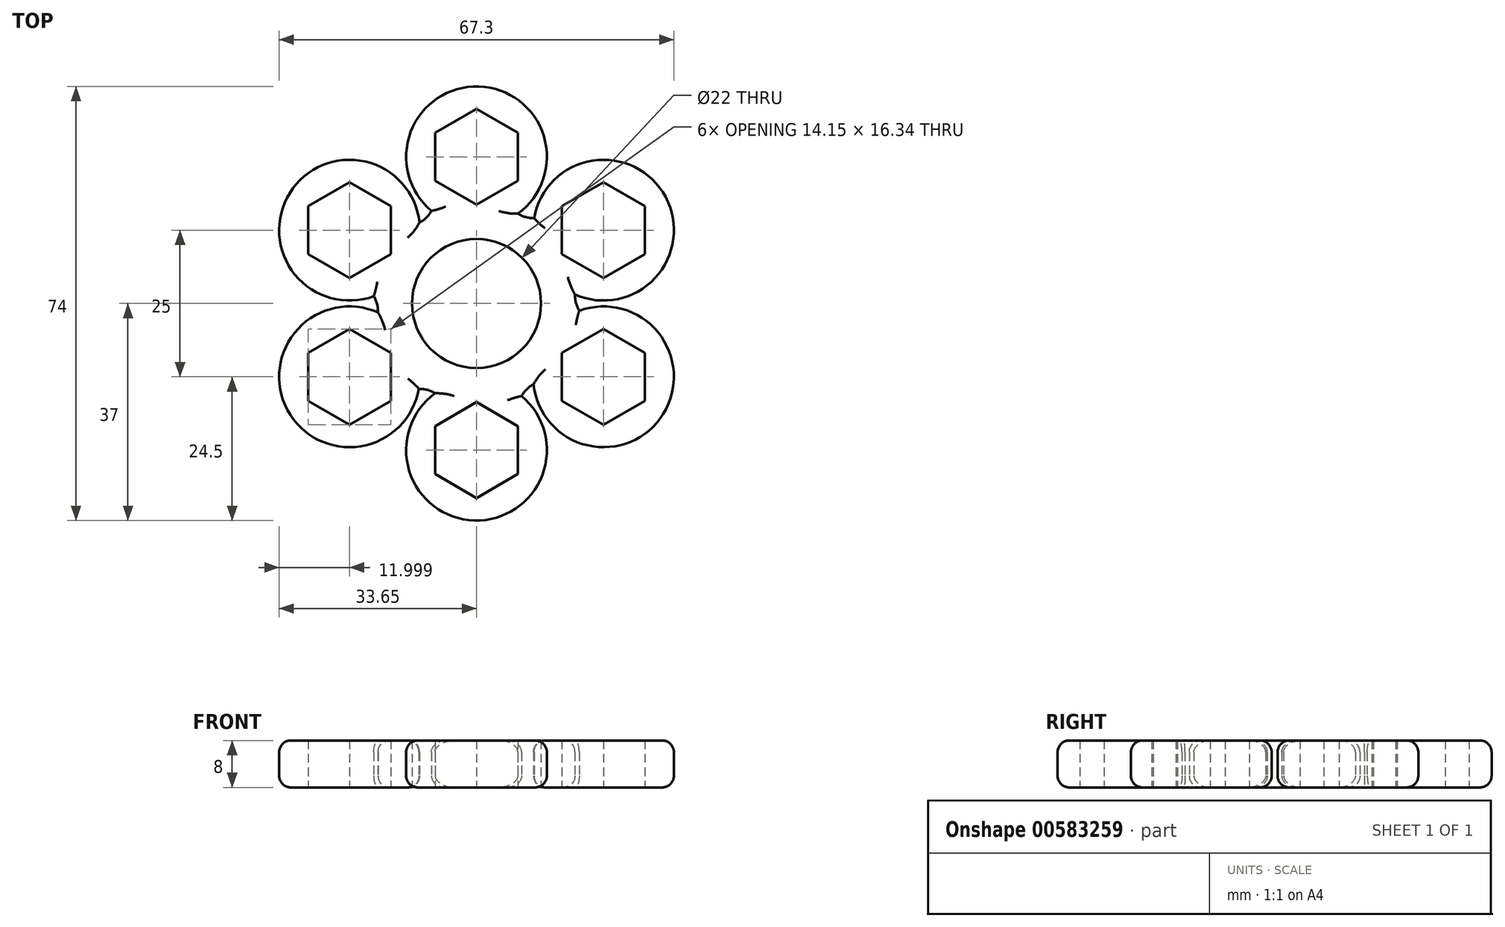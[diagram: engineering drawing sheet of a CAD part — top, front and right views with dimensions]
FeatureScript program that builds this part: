
annotation { "Feature Type Name" : "Feature", "Feature Type Description" : "" }
export const myFeature = defineFeature(function(context is Context, id is Id, definition is map)
    precondition{}
    {
        {
            var Q0;
            Q0=qCreatedBy(makeId("Top.planeOp"),FACE);
            var sketch = newSketch(context, id + "F0", { "sketchPlane" : qUnion([Q0])});
            skCircle(sketch, "E0", {"center": v(0, 0) * mm, "radius": 11 * mm});
            skCircle(sketch, "E1.cCircle", {"center": v(0, 25) * mm, "radius": 7.07 * mm, "construction": true});
            skLineSegment(sketch, "E1.0", {"start": v(7.07, 20.92) * mm, "end": v(0, 16.83) * mm});
            skLineSegment(sketch, "E1.1", {"start": v(0, 16.83) * mm, "end": v(-7.08, 20.92) * mm});
            skLineSegment(sketch, "E1.2", {"start": v(-7.08, 20.92) * mm, "end": v(-7.08, 29.08) * mm});
            skLineSegment(sketch, "E1.3", {"start": v(-7.08, 29.08) * mm, "end": v(0, 33.17) * mm});
            skLineSegment(sketch, "E1.4", {"start": v(0, 33.17) * mm, "end": v(7.08, 29.08) * mm});
            skLineSegment(sketch, "E1.5", {"start": v(7.07, 29.08) * mm, "end": v(7.07, 20.92) * mm});
            skPoint(sketch, "E1.0.midPoint", {"position": v(3.54, 18.87) * mm});
            skArc(sketch, "E2", {"start": v(7.08, 15.3) * mm, "mid": v(0, 37) * mm, "end": v(-7.08, 15.3) * mm});
            skLineSegment(sketch, "E3", {"start": v(-7.08, 15.3) * mm, "end": v(-7.08, 12.25) * mm});
            skLineSegment(sketch, "E4", {"start": v(7.08, 12.25) * mm, "end": v(7.08, 15.3) * mm});
            skPoint(sketch, "E5.orphan", {"position": v(7.07, 8.42) * mm});
            skLineSegment(sketch, "E6.1.0", {"start": v(-16.8, 1.53) * mm, "end": v(-14.15, 0) * mm});
            skArc(sketch, "E6.1.1", {"start": v(-9.72, 13.78) * mm, "mid": v(-32.04, 18.5) * mm, "end": v(-16.8, 1.53) * mm});
            skLineSegment(sketch, "E6.1.2", {"start": v(-7.08, 12.25) * mm, "end": v(-9.72, 13.78) * mm});
            skLineSegment(sketch, "E6.1.3", {"start": v(-14.58, 16.58) * mm, "end": v(-14.58, 8.42) * mm});
            skLineSegment(sketch, "E6.1.4", {"start": v(-14.58, 8.42) * mm, "end": v(-21.65, 4.33) * mm});
            skLineSegment(sketch, "E6.1.5", {"start": v(-21.65, 4.33) * mm, "end": v(-28.73, 8.42) * mm});
            skLineSegment(sketch, "E6.1.6", {"start": v(-28.73, 8.42) * mm, "end": v(-28.73, 16.58) * mm});
            skLineSegment(sketch, "E6.1.7", {"start": v(-28.73, 16.58) * mm, "end": v(-21.65, 20.67) * mm});
            skLineSegment(sketch, "E6.1.8", {"start": v(-21.65, 20.67) * mm, "end": v(-14.58, 16.58) * mm});
            skLineSegment(sketch, "E6.2.0", {"start": v(-9.72, -13.78) * mm, "end": v(-7.08, -12.25) * mm});
            skArc(sketch, "E6.2.1", {"start": v(-16.8, -1.53) * mm, "mid": v(-32.04, -18.5) * mm, "end": v(-9.72, -13.78) * mm});
            skLineSegment(sketch, "E6.2.2", {"start": v(-14.15, 0) * mm, "end": v(-16.8, -1.53) * mm});
            skLineSegment(sketch, "E6.2.3", {"start": v(-21.65, -4.33) * mm, "end": v(-14.58, -8.42) * mm});
            skLineSegment(sketch, "E6.2.4", {"start": v(-14.58, -8.42) * mm, "end": v(-14.58, -16.58) * mm});
            skLineSegment(sketch, "E6.2.5", {"start": v(-14.58, -16.58) * mm, "end": v(-21.65, -20.67) * mm});
            skLineSegment(sketch, "E6.2.6", {"start": v(-21.65, -20.67) * mm, "end": v(-28.73, -16.58) * mm});
            skLineSegment(sketch, "E6.2.7", {"start": v(-28.73, -16.58) * mm, "end": v(-28.73, -8.42) * mm});
            skLineSegment(sketch, "E6.2.8", {"start": v(-28.73, -8.42) * mm, "end": v(-21.65, -4.33) * mm});
            skLineSegment(sketch, "E6.3.0", {"start": v(7.08, -15.3) * mm, "end": v(7.08, -12.25) * mm});
            skArc(sketch, "E6.3.1", {"start": v(-7.08, -15.3) * mm, "mid": v(0, -37) * mm, "end": v(7.07, -15.3) * mm});
            skLineSegment(sketch, "E6.3.2", {"start": v(-7.08, -12.25) * mm, "end": v(-7.08, -15.3) * mm});
            skLineSegment(sketch, "E6.3.3", {"start": v(-7.08, -20.92) * mm, "end": v(0, -16.83) * mm});
            skLineSegment(sketch, "E6.3.4", {"start": v(0, -16.83) * mm, "end": v(7.07, -20.92) * mm});
            skLineSegment(sketch, "E6.3.5", {"start": v(7.08, -20.92) * mm, "end": v(7.08, -29.08) * mm});
            skLineSegment(sketch, "E6.3.6", {"start": v(7.07, -29.08) * mm, "end": v(0, -33.17) * mm});
            skLineSegment(sketch, "E6.3.7", {"start": v(0, -33.17) * mm, "end": v(-7.08, -29.08) * mm});
            skLineSegment(sketch, "E6.3.8", {"start": v(-7.08, -29.08) * mm, "end": v(-7.08, -20.92) * mm});
            skLineSegment(sketch, "E6.4.0", {"start": v(16.8, -1.53) * mm, "end": v(14.15, 0) * mm});
            skArc(sketch, "E6.4.1", {"start": v(9.72, -13.78) * mm, "mid": v(32.04, -18.5) * mm, "end": v(16.8, -1.53) * mm});
            skLineSegment(sketch, "E6.4.2", {"start": v(7.08, -12.25) * mm, "end": v(9.72, -13.78) * mm});
            skLineSegment(sketch, "E6.4.3", {"start": v(14.58, -16.58) * mm, "end": v(14.58, -8.42) * mm});
            skLineSegment(sketch, "E6.4.4", {"start": v(14.58, -8.42) * mm, "end": v(21.65, -4.33) * mm});
            skLineSegment(sketch, "E6.4.5", {"start": v(21.65, -4.33) * mm, "end": v(28.73, -8.42) * mm});
            skLineSegment(sketch, "E6.4.6", {"start": v(28.73, -8.42) * mm, "end": v(28.73, -16.58) * mm});
            skLineSegment(sketch, "E6.4.7", {"start": v(28.73, -16.58) * mm, "end": v(21.65, -20.67) * mm});
            skLineSegment(sketch, "E6.4.8", {"start": v(21.65, -20.67) * mm, "end": v(14.58, -16.58) * mm});
            skLineSegment(sketch, "E6.5.0", {"start": v(9.72, 13.78) * mm, "end": v(7.08, 12.25) * mm});
            skArc(sketch, "E6.5.1", {"start": v(16.8, 1.53) * mm, "mid": v(32.04, 18.5) * mm, "end": v(9.72, 13.78) * mm});
            skLineSegment(sketch, "E6.5.2", {"start": v(14.15, 0) * mm, "end": v(16.8, 1.53) * mm});
            skLineSegment(sketch, "E6.5.3", {"start": v(21.65, 4.33) * mm, "end": v(14.58, 8.42) * mm});
            skLineSegment(sketch, "E6.5.4", {"start": v(14.58, 8.42) * mm, "end": v(14.58, 16.58) * mm});
            skLineSegment(sketch, "E6.5.5", {"start": v(14.58, 16.58) * mm, "end": v(21.65, 20.67) * mm});
            skLineSegment(sketch, "E6.5.6", {"start": v(21.65, 20.67) * mm, "end": v(28.73, 16.58) * mm});
            skLineSegment(sketch, "E6.5.7", {"start": v(28.73, 16.58) * mm, "end": v(28.73, 8.42) * mm});
            skLineSegment(sketch, "E6.5.8", {"start": v(28.73, 8.42) * mm, "end": v(21.65, 4.33) * mm});
            skPoint(sketch, "E7.orphan", {"position": v(6.92, 12.17) * mm});
            skPoint(sketch, "E8.orphan", {"position": v(7.08, 12.08) * mm});
            skPoint(sketch, "E9.orphan", {"position": v(14, -0.09) * mm});
            skPoint(sketch, "E10.orphan", {"position": v(7.08, -12.08) * mm});
            skPoint(sketch, "E11.orphan", {"position": v(-14, 0.09) * mm});
            skSolve(sketch);
        }
        {
            var Q0;
            Q0=makeQuery(id+"F0.imprint","IMPRINT",FACE,{"disambiguationData":[TD([[makeQuery(id+"F0.imprint","IMPRINT",EDGE,{"derivedFrom":sQuery(id+"F0.wireOp",EDGE,"E0")}),-1.0]])]});
            extrude(context, id + "F1", {"entities" : qUnion([Q0]), "depth" : 8 * mm, "offsetDistance" : 25 * mm});
        }
        {
            var Q0;
            Q0=makeQuery(id+"F1.opExtrude","SWEPT_EDGE",EDGE,{"disambiguationData":[OSD([sQuery(id+"F0.wireOp",EDGE,"E3"),sQuery(id+"F0.wireOp",EDGE,"E6.1.2")])]});
            var Q1;
            Q1=makeQuery(id+"F1.opExtrude","SWEPT_EDGE",EDGE,{"disambiguationData":[OSD([sQuery(id+"F0.wireOp",EDGE,"E4"),sQuery(id+"F0.wireOp",EDGE,"E6.5.0")])]});
            var Q2;
            Q2=makeQuery(id+"F1.opExtrude","SWEPT_EDGE",EDGE,{"disambiguationData":[OSD([sQuery(id+"F0.wireOp",EDGE,"E6.4.0"),sQuery(id+"F0.wireOp",EDGE,"E6.5.2")])]});
            var Q3;
            Q3=makeQuery(id+"F1.opExtrude","SWEPT_EDGE",EDGE,{"disambiguationData":[OSD([sQuery(id+"F0.wireOp",EDGE,"E6.2.0"),sQuery(id+"F0.wireOp",EDGE,"E6.3.2")])]});
            var Q4;
            Q4=makeQuery(id+"F1.opExtrude","SWEPT_EDGE",EDGE,{"disambiguationData":[OSD([sQuery(id+"F0.wireOp",EDGE,"E6.1.0"),sQuery(id+"F0.wireOp",EDGE,"E6.2.2")])]});
            var Q5;
            Q5=makeQuery(id+"F1.opExtrude","SWEPT_EDGE",EDGE,{"disambiguationData":[OSD([sQuery(id+"F0.wireOp",EDGE,"E6.3.0"),sQuery(id+"F0.wireOp",EDGE,"E6.4.2")])]});
            fillet(context, id + "F2", {"entities" : qUnion([Q0, Q1, Q2, Q3, Q4, Q5]), "radius" : 5 * mm, "tangentPropagation" : true, "allowEdgeOverflow" : false});
        }
        {
            var Q0;
            Q0=makeQuery(id+"F1.opExtrude","CAP_EDGE",EDGE,{"disambiguationData":[OSD([sQuery(id+"F0.wireOp",EDGE,"E6.4.1")])],"isStart":false});
            var Q1;
            Q1=makeQuery(id+"F1.opExtrude","CAP_EDGE",EDGE,{"disambiguationData":[OSD([sQuery(id+"F0.wireOp",EDGE,"E6.3.1")])],"isStart":false});
            var Q2;
            Q2=makeQuery(id+"F1.opExtrude","CAP_EDGE",EDGE,{"disambiguationData":[OSD([sQuery(id+"F0.wireOp",EDGE,"E6.2.1")])],"isStart":false});
            var Q3;
            Q3=makeQuery(id+"F1.opExtrude","CAP_EDGE",EDGE,{"disambiguationData":[OSD([sQuery(id+"F0.wireOp",EDGE,"E6.1.1")])],"isStart":false});
            var Q4;
            Q4=makeQuery(id+"F1.opExtrude","CAP_EDGE",EDGE,{"disambiguationData":[OSD([sQuery(id+"F0.wireOp",EDGE,"E2")])],"isStart":true});
            var Q5;
            Q5=makeQuery(id+"F1.opExtrude","CAP_EDGE",EDGE,{"disambiguationData":[OSD([sQuery(id+"F0.wireOp",EDGE,"E6.5.1")])],"isStart":false});
            var Q6;
            Q6=makeQuery(id+"F1.opExtrude","CAP_EDGE",EDGE,{"disambiguationData":[OSD([sQuery(id+"F0.wireOp",EDGE,"E2")])],"isStart":false});
            var Q7;
            Q7=makeQuery(id+"F1.opExtrude","CAP_EDGE",EDGE,{"disambiguationData":[OSD([sQuery(id+"F0.wireOp",EDGE,"E6.5.1")])],"isStart":true});
            var Q8;
            Q8=makeQuery(id+"F1.opExtrude","CAP_EDGE",EDGE,{"disambiguationData":[OSD([sQuery(id+"F0.wireOp",EDGE,"E6.1.1")])],"isStart":true});
            var Q9;
            Q9=makeQuery(id+"F1.opExtrude","CAP_EDGE",EDGE,{"disambiguationData":[OSD([sQuery(id+"F0.wireOp",EDGE,"E6.4.1")])],"isStart":true});
            var Q10;
            Q10=makeQuery(id+"F1.opExtrude","CAP_EDGE",EDGE,{"disambiguationData":[OSD([sQuery(id+"F0.wireOp",EDGE,"E6.3.1")])],"isStart":true});
            var Q11;
            Q11=makeQuery(id+"F1.opExtrude","CAP_EDGE",EDGE,{"disambiguationData":[OSD([sQuery(id+"F0.wireOp",EDGE,"E6.2.1")])],"isStart":true});
            var Q12;
            {var subQ0=sQuery(id+"F0.wireOp",EDGE,"E6.3.2");var subQ1=sQuery(id+"F0.wireOp",EDGE,"E6.2.0");Q12=makeQuery(id+"F2.opFillet","BLEND_EDGE",EDGE,{"blendedFrom":[makeQuery(id+"F1.opExtrude","SWEPT_EDGE",EDGE,{"disambiguationData":[OSD([subQ1,subQ0])]}),makeQuery(id+"F1.opExtrude","CAP_FACE",FACE,{"disambiguationData":[OSD([sQuery(id+"F0.wireOp",EDGE,"E0"),sQuery(id+"F0.wireOp",EDGE,"E1.0"),sQuery(id+"F0.wireOp",EDGE,"E1.1"),sQuery(id+"F0.wireOp",EDGE,"E1.2"),sQuery(id+"F0.wireOp",EDGE,"E1.3"),sQuery(id+"F0.wireOp",EDGE,"E1.4"),sQuery(id+"F0.wireOp",EDGE,"E1.5"),sQuery(id+"F0.wireOp",EDGE,"E2"),sQuery(id+"F0.wireOp",EDGE,"E3"),sQuery(id+"F0.wireOp",EDGE,"E4"),sQuery(id+"F0.wireOp",EDGE,"E6.1.0"),sQuery(id+"F0.wireOp",EDGE,"E6.1.1"),sQuery(id+"F0.wireOp",EDGE,"E6.1.2"),sQuery(id+"F0.wireOp",EDGE,"E6.1.3"),sQuery(id+"F0.wireOp",EDGE,"E6.1.4"),sQuery(id+"F0.wireOp",EDGE,"E6.1.5"),sQuery(id+"F0.wireOp",EDGE,"E6.1.6"),sQuery(id+"F0.wireOp",EDGE,"E6.1.7"),sQuery(id+"F0.wireOp",EDGE,"E6.1.8"),subQ1,sQuery(id+"F0.wireOp",EDGE,"E6.2.1"),sQuery(id+"F0.wireOp",EDGE,"E6.2.2"),sQuery(id+"F0.wireOp",EDGE,"E6.2.3"),sQuery(id+"F0.wireOp",EDGE,"E6.2.4"),sQuery(id+"F0.wireOp",EDGE,"E6.2.5"),sQuery(id+"F0.wireOp",EDGE,"E6.2.6"),sQuery(id+"F0.wireOp",EDGE,"E6.2.7"),sQuery(id+"F0.wireOp",EDGE,"E6.2.8"),sQuery(id+"F0.wireOp",EDGE,"E6.3.0"),sQuery(id+"F0.wireOp",EDGE,"E6.3.1"),subQ0,sQuery(id+"F0.wireOp",EDGE,"E6.3.3"),sQuery(id+"F0.wireOp",EDGE,"E6.3.4"),sQuery(id+"F0.wireOp",EDGE,"E6.3.5"),sQuery(id+"F0.wireOp",EDGE,"E6.3.6"),sQuery(id+"F0.wireOp",EDGE,"E6.3.7"),sQuery(id+"F0.wireOp",EDGE,"E6.3.8"),sQuery(id+"F0.wireOp",EDGE,"E6.4.0"),sQuery(id+"F0.wireOp",EDGE,"E6.4.1"),sQuery(id+"F0.wireOp",EDGE,"E6.4.2"),sQuery(id+"F0.wireOp",EDGE,"E6.4.3"),sQuery(id+"F0.wireOp",EDGE,"E6.4.4"),sQuery(id+"F0.wireOp",EDGE,"E6.4.5"),sQuery(id+"F0.wireOp",EDGE,"E6.4.6"),sQuery(id+"F0.wireOp",EDGE,"E6.4.7"),sQuery(id+"F0.wireOp",EDGE,"E6.4.8"),sQuery(id+"F0.wireOp",EDGE,"E6.5.0"),sQuery(id+"F0.wireOp",EDGE,"E6.5.1"),sQuery(id+"F0.wireOp",EDGE,"E6.5.2"),sQuery(id+"F0.wireOp",EDGE,"E6.5.3"),sQuery(id+"F0.wireOp",EDGE,"E6.5.4"),sQuery(id+"F0.wireOp",EDGE,"E6.5.5"),sQuery(id+"F0.wireOp",EDGE,"E6.5.6"),sQuery(id+"F0.wireOp",EDGE,"E6.5.7"),sQuery(id+"F0.wireOp",EDGE,"E6.5.8")])],"isStart":false})],"blendedInto":[makeQuery(id+"F1.opExtrude","CAP_FACE",FACE,{"disambiguationData":[OSD([sQuery(id+"F0.wireOp",EDGE,"E0"),sQuery(id+"F0.wireOp",EDGE,"E1.0"),sQuery(id+"F0.wireOp",EDGE,"E1.1"),sQuery(id+"F0.wireOp",EDGE,"E1.2"),sQuery(id+"F0.wireOp",EDGE,"E1.3"),sQuery(id+"F0.wireOp",EDGE,"E1.4"),sQuery(id+"F0.wireOp",EDGE,"E1.5"),sQuery(id+"F0.wireOp",EDGE,"E2"),sQuery(id+"F0.wireOp",EDGE,"E3"),sQuery(id+"F0.wireOp",EDGE,"E4"),sQuery(id+"F0.wireOp",EDGE,"E6.1.0"),sQuery(id+"F0.wireOp",EDGE,"E6.1.1"),sQuery(id+"F0.wireOp",EDGE,"E6.1.2"),sQuery(id+"F0.wireOp",EDGE,"E6.1.3"),sQuery(id+"F0.wireOp",EDGE,"E6.1.4"),sQuery(id+"F0.wireOp",EDGE,"E6.1.5"),sQuery(id+"F0.wireOp",EDGE,"E6.1.6"),sQuery(id+"F0.wireOp",EDGE,"E6.1.7"),sQuery(id+"F0.wireOp",EDGE,"E6.1.8"),subQ1,sQuery(id+"F0.wireOp",EDGE,"E6.2.1"),sQuery(id+"F0.wireOp",EDGE,"E6.2.2"),sQuery(id+"F0.wireOp",EDGE,"E6.2.3"),sQuery(id+"F0.wireOp",EDGE,"E6.2.4"),sQuery(id+"F0.wireOp",EDGE,"E6.2.5"),sQuery(id+"F0.wireOp",EDGE,"E6.2.6"),sQuery(id+"F0.wireOp",EDGE,"E6.2.7"),sQuery(id+"F0.wireOp",EDGE,"E6.2.8"),sQuery(id+"F0.wireOp",EDGE,"E6.3.0"),sQuery(id+"F0.wireOp",EDGE,"E6.3.1"),subQ0,sQuery(id+"F0.wireOp",EDGE,"E6.3.3"),sQuery(id+"F0.wireOp",EDGE,"E6.3.4"),sQuery(id+"F0.wireOp",EDGE,"E6.3.5"),sQuery(id+"F0.wireOp",EDGE,"E6.3.6"),sQuery(id+"F0.wireOp",EDGE,"E6.3.7"),sQuery(id+"F0.wireOp",EDGE,"E6.3.8"),sQuery(id+"F0.wireOp",EDGE,"E6.4.0"),sQuery(id+"F0.wireOp",EDGE,"E6.4.1"),sQuery(id+"F0.wireOp",EDGE,"E6.4.2"),sQuery(id+"F0.wireOp",EDGE,"E6.4.3"),sQuery(id+"F0.wireOp",EDGE,"E6.4.4"),sQuery(id+"F0.wireOp",EDGE,"E6.4.5"),sQuery(id+"F0.wireOp",EDGE,"E6.4.6"),sQuery(id+"F0.wireOp",EDGE,"E6.4.7"),sQuery(id+"F0.wireOp",EDGE,"E6.4.8"),sQuery(id+"F0.wireOp",EDGE,"E6.5.0"),sQuery(id+"F0.wireOp",EDGE,"E6.5.1"),sQuery(id+"F0.wireOp",EDGE,"E6.5.2"),sQuery(id+"F0.wireOp",EDGE,"E6.5.3"),sQuery(id+"F0.wireOp",EDGE,"E6.5.4"),sQuery(id+"F0.wireOp",EDGE,"E6.5.5"),sQuery(id+"F0.wireOp",EDGE,"E6.5.6"),sQuery(id+"F0.wireOp",EDGE,"E6.5.7"),sQuery(id+"F0.wireOp",EDGE,"E6.5.8")])],"isStart":false})]});}
            var Q13;
            {var subQ0=sQuery(id+"F0.wireOp",EDGE,"E6.4.2");var subQ1=sQuery(id+"F0.wireOp",EDGE,"E6.3.0");Q13=makeQuery(id+"F2.opFillet","BLEND_EDGE",EDGE,{"blendedFrom":[makeQuery(id+"F1.opExtrude","SWEPT_EDGE",EDGE,{"disambiguationData":[OSD([subQ1,subQ0])]}),makeQuery(id+"F1.opExtrude","CAP_FACE",FACE,{"disambiguationData":[OSD([sQuery(id+"F0.wireOp",EDGE,"E0"),sQuery(id+"F0.wireOp",EDGE,"E1.0"),sQuery(id+"F0.wireOp",EDGE,"E1.1"),sQuery(id+"F0.wireOp",EDGE,"E1.2"),sQuery(id+"F0.wireOp",EDGE,"E1.3"),sQuery(id+"F0.wireOp",EDGE,"E1.4"),sQuery(id+"F0.wireOp",EDGE,"E1.5"),sQuery(id+"F0.wireOp",EDGE,"E2"),sQuery(id+"F0.wireOp",EDGE,"E3"),sQuery(id+"F0.wireOp",EDGE,"E4"),sQuery(id+"F0.wireOp",EDGE,"E6.1.0"),sQuery(id+"F0.wireOp",EDGE,"E6.1.1"),sQuery(id+"F0.wireOp",EDGE,"E6.1.2"),sQuery(id+"F0.wireOp",EDGE,"E6.1.3"),sQuery(id+"F0.wireOp",EDGE,"E6.1.4"),sQuery(id+"F0.wireOp",EDGE,"E6.1.5"),sQuery(id+"F0.wireOp",EDGE,"E6.1.6"),sQuery(id+"F0.wireOp",EDGE,"E6.1.7"),sQuery(id+"F0.wireOp",EDGE,"E6.1.8"),sQuery(id+"F0.wireOp",EDGE,"E6.2.0"),sQuery(id+"F0.wireOp",EDGE,"E6.2.1"),sQuery(id+"F0.wireOp",EDGE,"E6.2.2"),sQuery(id+"F0.wireOp",EDGE,"E6.2.3"),sQuery(id+"F0.wireOp",EDGE,"E6.2.4"),sQuery(id+"F0.wireOp",EDGE,"E6.2.5"),sQuery(id+"F0.wireOp",EDGE,"E6.2.6"),sQuery(id+"F0.wireOp",EDGE,"E6.2.7"),sQuery(id+"F0.wireOp",EDGE,"E6.2.8"),subQ1,sQuery(id+"F0.wireOp",EDGE,"E6.3.1"),sQuery(id+"F0.wireOp",EDGE,"E6.3.2"),sQuery(id+"F0.wireOp",EDGE,"E6.3.3"),sQuery(id+"F0.wireOp",EDGE,"E6.3.4"),sQuery(id+"F0.wireOp",EDGE,"E6.3.5"),sQuery(id+"F0.wireOp",EDGE,"E6.3.6"),sQuery(id+"F0.wireOp",EDGE,"E6.3.7"),sQuery(id+"F0.wireOp",EDGE,"E6.3.8"),sQuery(id+"F0.wireOp",EDGE,"E6.4.0"),sQuery(id+"F0.wireOp",EDGE,"E6.4.1"),subQ0,sQuery(id+"F0.wireOp",EDGE,"E6.4.3"),sQuery(id+"F0.wireOp",EDGE,"E6.4.4"),sQuery(id+"F0.wireOp",EDGE,"E6.4.5"),sQuery(id+"F0.wireOp",EDGE,"E6.4.6"),sQuery(id+"F0.wireOp",EDGE,"E6.4.7"),sQuery(id+"F0.wireOp",EDGE,"E6.4.8"),sQuery(id+"F0.wireOp",EDGE,"E6.5.0"),sQuery(id+"F0.wireOp",EDGE,"E6.5.1"),sQuery(id+"F0.wireOp",EDGE,"E6.5.2"),sQuery(id+"F0.wireOp",EDGE,"E6.5.3"),sQuery(id+"F0.wireOp",EDGE,"E6.5.4"),sQuery(id+"F0.wireOp",EDGE,"E6.5.5"),sQuery(id+"F0.wireOp",EDGE,"E6.5.6"),sQuery(id+"F0.wireOp",EDGE,"E6.5.7"),sQuery(id+"F0.wireOp",EDGE,"E6.5.8")])],"isStart":false})],"blendedInto":[makeQuery(id+"F1.opExtrude","CAP_FACE",FACE,{"disambiguationData":[OSD([sQuery(id+"F0.wireOp",EDGE,"E0"),sQuery(id+"F0.wireOp",EDGE,"E1.0"),sQuery(id+"F0.wireOp",EDGE,"E1.1"),sQuery(id+"F0.wireOp",EDGE,"E1.2"),sQuery(id+"F0.wireOp",EDGE,"E1.3"),sQuery(id+"F0.wireOp",EDGE,"E1.4"),sQuery(id+"F0.wireOp",EDGE,"E1.5"),sQuery(id+"F0.wireOp",EDGE,"E2"),sQuery(id+"F0.wireOp",EDGE,"E3"),sQuery(id+"F0.wireOp",EDGE,"E4"),sQuery(id+"F0.wireOp",EDGE,"E6.1.0"),sQuery(id+"F0.wireOp",EDGE,"E6.1.1"),sQuery(id+"F0.wireOp",EDGE,"E6.1.2"),sQuery(id+"F0.wireOp",EDGE,"E6.1.3"),sQuery(id+"F0.wireOp",EDGE,"E6.1.4"),sQuery(id+"F0.wireOp",EDGE,"E6.1.5"),sQuery(id+"F0.wireOp",EDGE,"E6.1.6"),sQuery(id+"F0.wireOp",EDGE,"E6.1.7"),sQuery(id+"F0.wireOp",EDGE,"E6.1.8"),sQuery(id+"F0.wireOp",EDGE,"E6.2.0"),sQuery(id+"F0.wireOp",EDGE,"E6.2.1"),sQuery(id+"F0.wireOp",EDGE,"E6.2.2"),sQuery(id+"F0.wireOp",EDGE,"E6.2.3"),sQuery(id+"F0.wireOp",EDGE,"E6.2.4"),sQuery(id+"F0.wireOp",EDGE,"E6.2.5"),sQuery(id+"F0.wireOp",EDGE,"E6.2.6"),sQuery(id+"F0.wireOp",EDGE,"E6.2.7"),sQuery(id+"F0.wireOp",EDGE,"E6.2.8"),subQ1,sQuery(id+"F0.wireOp",EDGE,"E6.3.1"),sQuery(id+"F0.wireOp",EDGE,"E6.3.2"),sQuery(id+"F0.wireOp",EDGE,"E6.3.3"),sQuery(id+"F0.wireOp",EDGE,"E6.3.4"),sQuery(id+"F0.wireOp",EDGE,"E6.3.5"),sQuery(id+"F0.wireOp",EDGE,"E6.3.6"),sQuery(id+"F0.wireOp",EDGE,"E6.3.7"),sQuery(id+"F0.wireOp",EDGE,"E6.3.8"),sQuery(id+"F0.wireOp",EDGE,"E6.4.0"),sQuery(id+"F0.wireOp",EDGE,"E6.4.1"),subQ0,sQuery(id+"F0.wireOp",EDGE,"E6.4.3"),sQuery(id+"F0.wireOp",EDGE,"E6.4.4"),sQuery(id+"F0.wireOp",EDGE,"E6.4.5"),sQuery(id+"F0.wireOp",EDGE,"E6.4.6"),sQuery(id+"F0.wireOp",EDGE,"E6.4.7"),sQuery(id+"F0.wireOp",EDGE,"E6.4.8"),sQuery(id+"F0.wireOp",EDGE,"E6.5.0"),sQuery(id+"F0.wireOp",EDGE,"E6.5.1"),sQuery(id+"F0.wireOp",EDGE,"E6.5.2"),sQuery(id+"F0.wireOp",EDGE,"E6.5.3"),sQuery(id+"F0.wireOp",EDGE,"E6.5.4"),sQuery(id+"F0.wireOp",EDGE,"E6.5.5"),sQuery(id+"F0.wireOp",EDGE,"E6.5.6"),sQuery(id+"F0.wireOp",EDGE,"E6.5.7"),sQuery(id+"F0.wireOp",EDGE,"E6.5.8")])],"isStart":false})]});}
            var Q14;
            {var subQ0=sQuery(id+"F0.wireOp",EDGE,"E6.5.2");var subQ1=sQuery(id+"F0.wireOp",EDGE,"E6.4.0");Q14=makeQuery(id+"F2.opFillet","BLEND_EDGE",EDGE,{"blendedFrom":[makeQuery(id+"F1.opExtrude","SWEPT_EDGE",EDGE,{"disambiguationData":[OSD([subQ1,subQ0])]}),makeQuery(id+"F1.opExtrude","CAP_FACE",FACE,{"disambiguationData":[OSD([sQuery(id+"F0.wireOp",EDGE,"E0"),sQuery(id+"F0.wireOp",EDGE,"E1.0"),sQuery(id+"F0.wireOp",EDGE,"E1.1"),sQuery(id+"F0.wireOp",EDGE,"E1.2"),sQuery(id+"F0.wireOp",EDGE,"E1.3"),sQuery(id+"F0.wireOp",EDGE,"E1.4"),sQuery(id+"F0.wireOp",EDGE,"E1.5"),sQuery(id+"F0.wireOp",EDGE,"E2"),sQuery(id+"F0.wireOp",EDGE,"E3"),sQuery(id+"F0.wireOp",EDGE,"E4"),sQuery(id+"F0.wireOp",EDGE,"E6.1.0"),sQuery(id+"F0.wireOp",EDGE,"E6.1.1"),sQuery(id+"F0.wireOp",EDGE,"E6.1.2"),sQuery(id+"F0.wireOp",EDGE,"E6.1.3"),sQuery(id+"F0.wireOp",EDGE,"E6.1.4"),sQuery(id+"F0.wireOp",EDGE,"E6.1.5"),sQuery(id+"F0.wireOp",EDGE,"E6.1.6"),sQuery(id+"F0.wireOp",EDGE,"E6.1.7"),sQuery(id+"F0.wireOp",EDGE,"E6.1.8"),sQuery(id+"F0.wireOp",EDGE,"E6.2.0"),sQuery(id+"F0.wireOp",EDGE,"E6.2.1"),sQuery(id+"F0.wireOp",EDGE,"E6.2.2"),sQuery(id+"F0.wireOp",EDGE,"E6.2.3"),sQuery(id+"F0.wireOp",EDGE,"E6.2.4"),sQuery(id+"F0.wireOp",EDGE,"E6.2.5"),sQuery(id+"F0.wireOp",EDGE,"E6.2.6"),sQuery(id+"F0.wireOp",EDGE,"E6.2.7"),sQuery(id+"F0.wireOp",EDGE,"E6.2.8"),sQuery(id+"F0.wireOp",EDGE,"E6.3.0"),sQuery(id+"F0.wireOp",EDGE,"E6.3.1"),sQuery(id+"F0.wireOp",EDGE,"E6.3.2"),sQuery(id+"F0.wireOp",EDGE,"E6.3.3"),sQuery(id+"F0.wireOp",EDGE,"E6.3.4"),sQuery(id+"F0.wireOp",EDGE,"E6.3.5"),sQuery(id+"F0.wireOp",EDGE,"E6.3.6"),sQuery(id+"F0.wireOp",EDGE,"E6.3.7"),sQuery(id+"F0.wireOp",EDGE,"E6.3.8"),subQ1,sQuery(id+"F0.wireOp",EDGE,"E6.4.1"),sQuery(id+"F0.wireOp",EDGE,"E6.4.2"),sQuery(id+"F0.wireOp",EDGE,"E6.4.3"),sQuery(id+"F0.wireOp",EDGE,"E6.4.4"),sQuery(id+"F0.wireOp",EDGE,"E6.4.5"),sQuery(id+"F0.wireOp",EDGE,"E6.4.6"),sQuery(id+"F0.wireOp",EDGE,"E6.4.7"),sQuery(id+"F0.wireOp",EDGE,"E6.4.8"),sQuery(id+"F0.wireOp",EDGE,"E6.5.0"),sQuery(id+"F0.wireOp",EDGE,"E6.5.1"),subQ0,sQuery(id+"F0.wireOp",EDGE,"E6.5.3"),sQuery(id+"F0.wireOp",EDGE,"E6.5.4"),sQuery(id+"F0.wireOp",EDGE,"E6.5.5"),sQuery(id+"F0.wireOp",EDGE,"E6.5.6"),sQuery(id+"F0.wireOp",EDGE,"E6.5.7"),sQuery(id+"F0.wireOp",EDGE,"E6.5.8")])],"isStart":false})],"blendedInto":[makeQuery(id+"F1.opExtrude","CAP_FACE",FACE,{"disambiguationData":[OSD([sQuery(id+"F0.wireOp",EDGE,"E0"),sQuery(id+"F0.wireOp",EDGE,"E1.0"),sQuery(id+"F0.wireOp",EDGE,"E1.1"),sQuery(id+"F0.wireOp",EDGE,"E1.2"),sQuery(id+"F0.wireOp",EDGE,"E1.3"),sQuery(id+"F0.wireOp",EDGE,"E1.4"),sQuery(id+"F0.wireOp",EDGE,"E1.5"),sQuery(id+"F0.wireOp",EDGE,"E2"),sQuery(id+"F0.wireOp",EDGE,"E3"),sQuery(id+"F0.wireOp",EDGE,"E4"),sQuery(id+"F0.wireOp",EDGE,"E6.1.0"),sQuery(id+"F0.wireOp",EDGE,"E6.1.1"),sQuery(id+"F0.wireOp",EDGE,"E6.1.2"),sQuery(id+"F0.wireOp",EDGE,"E6.1.3"),sQuery(id+"F0.wireOp",EDGE,"E6.1.4"),sQuery(id+"F0.wireOp",EDGE,"E6.1.5"),sQuery(id+"F0.wireOp",EDGE,"E6.1.6"),sQuery(id+"F0.wireOp",EDGE,"E6.1.7"),sQuery(id+"F0.wireOp",EDGE,"E6.1.8"),sQuery(id+"F0.wireOp",EDGE,"E6.2.0"),sQuery(id+"F0.wireOp",EDGE,"E6.2.1"),sQuery(id+"F0.wireOp",EDGE,"E6.2.2"),sQuery(id+"F0.wireOp",EDGE,"E6.2.3"),sQuery(id+"F0.wireOp",EDGE,"E6.2.4"),sQuery(id+"F0.wireOp",EDGE,"E6.2.5"),sQuery(id+"F0.wireOp",EDGE,"E6.2.6"),sQuery(id+"F0.wireOp",EDGE,"E6.2.7"),sQuery(id+"F0.wireOp",EDGE,"E6.2.8"),sQuery(id+"F0.wireOp",EDGE,"E6.3.0"),sQuery(id+"F0.wireOp",EDGE,"E6.3.1"),sQuery(id+"F0.wireOp",EDGE,"E6.3.2"),sQuery(id+"F0.wireOp",EDGE,"E6.3.3"),sQuery(id+"F0.wireOp",EDGE,"E6.3.4"),sQuery(id+"F0.wireOp",EDGE,"E6.3.5"),sQuery(id+"F0.wireOp",EDGE,"E6.3.6"),sQuery(id+"F0.wireOp",EDGE,"E6.3.7"),sQuery(id+"F0.wireOp",EDGE,"E6.3.8"),subQ1,sQuery(id+"F0.wireOp",EDGE,"E6.4.1"),sQuery(id+"F0.wireOp",EDGE,"E6.4.2"),sQuery(id+"F0.wireOp",EDGE,"E6.4.3"),sQuery(id+"F0.wireOp",EDGE,"E6.4.4"),sQuery(id+"F0.wireOp",EDGE,"E6.4.5"),sQuery(id+"F0.wireOp",EDGE,"E6.4.6"),sQuery(id+"F0.wireOp",EDGE,"E6.4.7"),sQuery(id+"F0.wireOp",EDGE,"E6.4.8"),sQuery(id+"F0.wireOp",EDGE,"E6.5.0"),sQuery(id+"F0.wireOp",EDGE,"E6.5.1"),subQ0,sQuery(id+"F0.wireOp",EDGE,"E6.5.3"),sQuery(id+"F0.wireOp",EDGE,"E6.5.4"),sQuery(id+"F0.wireOp",EDGE,"E6.5.5"),sQuery(id+"F0.wireOp",EDGE,"E6.5.6"),sQuery(id+"F0.wireOp",EDGE,"E6.5.7"),sQuery(id+"F0.wireOp",EDGE,"E6.5.8")])],"isStart":false})]});}
            var Q15;
            {var subQ0=sQuery(id+"F0.wireOp",EDGE,"E6.5.0");var subQ1=sQuery(id+"F0.wireOp",EDGE,"E4");Q15=makeQuery(id+"F2.opFillet","BLEND_EDGE",EDGE,{"blendedFrom":[makeQuery(id+"F1.opExtrude","SWEPT_EDGE",EDGE,{"disambiguationData":[OSD([subQ1,subQ0])]}),makeQuery(id+"F1.opExtrude","CAP_FACE",FACE,{"disambiguationData":[OSD([sQuery(id+"F0.wireOp",EDGE,"E0"),sQuery(id+"F0.wireOp",EDGE,"E1.0"),sQuery(id+"F0.wireOp",EDGE,"E1.1"),sQuery(id+"F0.wireOp",EDGE,"E1.2"),sQuery(id+"F0.wireOp",EDGE,"E1.3"),sQuery(id+"F0.wireOp",EDGE,"E1.4"),sQuery(id+"F0.wireOp",EDGE,"E1.5"),sQuery(id+"F0.wireOp",EDGE,"E2"),sQuery(id+"F0.wireOp",EDGE,"E3"),subQ1,sQuery(id+"F0.wireOp",EDGE,"E6.1.0"),sQuery(id+"F0.wireOp",EDGE,"E6.1.1"),sQuery(id+"F0.wireOp",EDGE,"E6.1.2"),sQuery(id+"F0.wireOp",EDGE,"E6.1.3"),sQuery(id+"F0.wireOp",EDGE,"E6.1.4"),sQuery(id+"F0.wireOp",EDGE,"E6.1.5"),sQuery(id+"F0.wireOp",EDGE,"E6.1.6"),sQuery(id+"F0.wireOp",EDGE,"E6.1.7"),sQuery(id+"F0.wireOp",EDGE,"E6.1.8"),sQuery(id+"F0.wireOp",EDGE,"E6.2.0"),sQuery(id+"F0.wireOp",EDGE,"E6.2.1"),sQuery(id+"F0.wireOp",EDGE,"E6.2.2"),sQuery(id+"F0.wireOp",EDGE,"E6.2.3"),sQuery(id+"F0.wireOp",EDGE,"E6.2.4"),sQuery(id+"F0.wireOp",EDGE,"E6.2.5"),sQuery(id+"F0.wireOp",EDGE,"E6.2.6"),sQuery(id+"F0.wireOp",EDGE,"E6.2.7"),sQuery(id+"F0.wireOp",EDGE,"E6.2.8"),sQuery(id+"F0.wireOp",EDGE,"E6.3.0"),sQuery(id+"F0.wireOp",EDGE,"E6.3.1"),sQuery(id+"F0.wireOp",EDGE,"E6.3.2"),sQuery(id+"F0.wireOp",EDGE,"E6.3.3"),sQuery(id+"F0.wireOp",EDGE,"E6.3.4"),sQuery(id+"F0.wireOp",EDGE,"E6.3.5"),sQuery(id+"F0.wireOp",EDGE,"E6.3.6"),sQuery(id+"F0.wireOp",EDGE,"E6.3.7"),sQuery(id+"F0.wireOp",EDGE,"E6.3.8"),sQuery(id+"F0.wireOp",EDGE,"E6.4.0"),sQuery(id+"F0.wireOp",EDGE,"E6.4.1"),sQuery(id+"F0.wireOp",EDGE,"E6.4.2"),sQuery(id+"F0.wireOp",EDGE,"E6.4.3"),sQuery(id+"F0.wireOp",EDGE,"E6.4.4"),sQuery(id+"F0.wireOp",EDGE,"E6.4.5"),sQuery(id+"F0.wireOp",EDGE,"E6.4.6"),sQuery(id+"F0.wireOp",EDGE,"E6.4.7"),sQuery(id+"F0.wireOp",EDGE,"E6.4.8"),subQ0,sQuery(id+"F0.wireOp",EDGE,"E6.5.1"),sQuery(id+"F0.wireOp",EDGE,"E6.5.2"),sQuery(id+"F0.wireOp",EDGE,"E6.5.3"),sQuery(id+"F0.wireOp",EDGE,"E6.5.4"),sQuery(id+"F0.wireOp",EDGE,"E6.5.5"),sQuery(id+"F0.wireOp",EDGE,"E6.5.6"),sQuery(id+"F0.wireOp",EDGE,"E6.5.7"),sQuery(id+"F0.wireOp",EDGE,"E6.5.8")])],"isStart":false})],"blendedInto":[makeQuery(id+"F1.opExtrude","CAP_FACE",FACE,{"disambiguationData":[OSD([sQuery(id+"F0.wireOp",EDGE,"E0"),sQuery(id+"F0.wireOp",EDGE,"E1.0"),sQuery(id+"F0.wireOp",EDGE,"E1.1"),sQuery(id+"F0.wireOp",EDGE,"E1.2"),sQuery(id+"F0.wireOp",EDGE,"E1.3"),sQuery(id+"F0.wireOp",EDGE,"E1.4"),sQuery(id+"F0.wireOp",EDGE,"E1.5"),sQuery(id+"F0.wireOp",EDGE,"E2"),sQuery(id+"F0.wireOp",EDGE,"E3"),subQ1,sQuery(id+"F0.wireOp",EDGE,"E6.1.0"),sQuery(id+"F0.wireOp",EDGE,"E6.1.1"),sQuery(id+"F0.wireOp",EDGE,"E6.1.2"),sQuery(id+"F0.wireOp",EDGE,"E6.1.3"),sQuery(id+"F0.wireOp",EDGE,"E6.1.4"),sQuery(id+"F0.wireOp",EDGE,"E6.1.5"),sQuery(id+"F0.wireOp",EDGE,"E6.1.6"),sQuery(id+"F0.wireOp",EDGE,"E6.1.7"),sQuery(id+"F0.wireOp",EDGE,"E6.1.8"),sQuery(id+"F0.wireOp",EDGE,"E6.2.0"),sQuery(id+"F0.wireOp",EDGE,"E6.2.1"),sQuery(id+"F0.wireOp",EDGE,"E6.2.2"),sQuery(id+"F0.wireOp",EDGE,"E6.2.3"),sQuery(id+"F0.wireOp",EDGE,"E6.2.4"),sQuery(id+"F0.wireOp",EDGE,"E6.2.5"),sQuery(id+"F0.wireOp",EDGE,"E6.2.6"),sQuery(id+"F0.wireOp",EDGE,"E6.2.7"),sQuery(id+"F0.wireOp",EDGE,"E6.2.8"),sQuery(id+"F0.wireOp",EDGE,"E6.3.0"),sQuery(id+"F0.wireOp",EDGE,"E6.3.1"),sQuery(id+"F0.wireOp",EDGE,"E6.3.2"),sQuery(id+"F0.wireOp",EDGE,"E6.3.3"),sQuery(id+"F0.wireOp",EDGE,"E6.3.4"),sQuery(id+"F0.wireOp",EDGE,"E6.3.5"),sQuery(id+"F0.wireOp",EDGE,"E6.3.6"),sQuery(id+"F0.wireOp",EDGE,"E6.3.7"),sQuery(id+"F0.wireOp",EDGE,"E6.3.8"),sQuery(id+"F0.wireOp",EDGE,"E6.4.0"),sQuery(id+"F0.wireOp",EDGE,"E6.4.1"),sQuery(id+"F0.wireOp",EDGE,"E6.4.2"),sQuery(id+"F0.wireOp",EDGE,"E6.4.3"),sQuery(id+"F0.wireOp",EDGE,"E6.4.4"),sQuery(id+"F0.wireOp",EDGE,"E6.4.5"),sQuery(id+"F0.wireOp",EDGE,"E6.4.6"),sQuery(id+"F0.wireOp",EDGE,"E6.4.7"),sQuery(id+"F0.wireOp",EDGE,"E6.4.8"),subQ0,sQuery(id+"F0.wireOp",EDGE,"E6.5.1"),sQuery(id+"F0.wireOp",EDGE,"E6.5.2"),sQuery(id+"F0.wireOp",EDGE,"E6.5.3"),sQuery(id+"F0.wireOp",EDGE,"E6.5.4"),sQuery(id+"F0.wireOp",EDGE,"E6.5.5"),sQuery(id+"F0.wireOp",EDGE,"E6.5.6"),sQuery(id+"F0.wireOp",EDGE,"E6.5.7"),sQuery(id+"F0.wireOp",EDGE,"E6.5.8")])],"isStart":false})]});}
            var Q16;
            {var subQ0=sQuery(id+"F0.wireOp",EDGE,"E6.1.2");var subQ1=sQuery(id+"F0.wireOp",EDGE,"E3");Q16=makeQuery(id+"F2.opFillet","BLEND_EDGE",EDGE,{"blendedFrom":[makeQuery(id+"F1.opExtrude","SWEPT_EDGE",EDGE,{"disambiguationData":[OSD([subQ1,subQ0])]}),makeQuery(id+"F1.opExtrude","CAP_FACE",FACE,{"disambiguationData":[OSD([sQuery(id+"F0.wireOp",EDGE,"E0"),sQuery(id+"F0.wireOp",EDGE,"E1.0"),sQuery(id+"F0.wireOp",EDGE,"E1.1"),sQuery(id+"F0.wireOp",EDGE,"E1.2"),sQuery(id+"F0.wireOp",EDGE,"E1.3"),sQuery(id+"F0.wireOp",EDGE,"E1.4"),sQuery(id+"F0.wireOp",EDGE,"E1.5"),sQuery(id+"F0.wireOp",EDGE,"E2"),subQ1,sQuery(id+"F0.wireOp",EDGE,"E4"),sQuery(id+"F0.wireOp",EDGE,"E6.1.0"),sQuery(id+"F0.wireOp",EDGE,"E6.1.1"),subQ0,sQuery(id+"F0.wireOp",EDGE,"E6.1.3"),sQuery(id+"F0.wireOp",EDGE,"E6.1.4"),sQuery(id+"F0.wireOp",EDGE,"E6.1.5"),sQuery(id+"F0.wireOp",EDGE,"E6.1.6"),sQuery(id+"F0.wireOp",EDGE,"E6.1.7"),sQuery(id+"F0.wireOp",EDGE,"E6.1.8"),sQuery(id+"F0.wireOp",EDGE,"E6.2.0"),sQuery(id+"F0.wireOp",EDGE,"E6.2.1"),sQuery(id+"F0.wireOp",EDGE,"E6.2.2"),sQuery(id+"F0.wireOp",EDGE,"E6.2.3"),sQuery(id+"F0.wireOp",EDGE,"E6.2.4"),sQuery(id+"F0.wireOp",EDGE,"E6.2.5"),sQuery(id+"F0.wireOp",EDGE,"E6.2.6"),sQuery(id+"F0.wireOp",EDGE,"E6.2.7"),sQuery(id+"F0.wireOp",EDGE,"E6.2.8"),sQuery(id+"F0.wireOp",EDGE,"E6.3.0"),sQuery(id+"F0.wireOp",EDGE,"E6.3.1"),sQuery(id+"F0.wireOp",EDGE,"E6.3.2"),sQuery(id+"F0.wireOp",EDGE,"E6.3.3"),sQuery(id+"F0.wireOp",EDGE,"E6.3.4"),sQuery(id+"F0.wireOp",EDGE,"E6.3.5"),sQuery(id+"F0.wireOp",EDGE,"E6.3.6"),sQuery(id+"F0.wireOp",EDGE,"E6.3.7"),sQuery(id+"F0.wireOp",EDGE,"E6.3.8"),sQuery(id+"F0.wireOp",EDGE,"E6.4.0"),sQuery(id+"F0.wireOp",EDGE,"E6.4.1"),sQuery(id+"F0.wireOp",EDGE,"E6.4.2"),sQuery(id+"F0.wireOp",EDGE,"E6.4.3"),sQuery(id+"F0.wireOp",EDGE,"E6.4.4"),sQuery(id+"F0.wireOp",EDGE,"E6.4.5"),sQuery(id+"F0.wireOp",EDGE,"E6.4.6"),sQuery(id+"F0.wireOp",EDGE,"E6.4.7"),sQuery(id+"F0.wireOp",EDGE,"E6.4.8"),sQuery(id+"F0.wireOp",EDGE,"E6.5.0"),sQuery(id+"F0.wireOp",EDGE,"E6.5.1"),sQuery(id+"F0.wireOp",EDGE,"E6.5.2"),sQuery(id+"F0.wireOp",EDGE,"E6.5.3"),sQuery(id+"F0.wireOp",EDGE,"E6.5.4"),sQuery(id+"F0.wireOp",EDGE,"E6.5.5"),sQuery(id+"F0.wireOp",EDGE,"E6.5.6"),sQuery(id+"F0.wireOp",EDGE,"E6.5.7"),sQuery(id+"F0.wireOp",EDGE,"E6.5.8")])],"isStart":false})],"blendedInto":[makeQuery(id+"F1.opExtrude","CAP_FACE",FACE,{"disambiguationData":[OSD([sQuery(id+"F0.wireOp",EDGE,"E0"),sQuery(id+"F0.wireOp",EDGE,"E1.0"),sQuery(id+"F0.wireOp",EDGE,"E1.1"),sQuery(id+"F0.wireOp",EDGE,"E1.2"),sQuery(id+"F0.wireOp",EDGE,"E1.3"),sQuery(id+"F0.wireOp",EDGE,"E1.4"),sQuery(id+"F0.wireOp",EDGE,"E1.5"),sQuery(id+"F0.wireOp",EDGE,"E2"),subQ1,sQuery(id+"F0.wireOp",EDGE,"E4"),sQuery(id+"F0.wireOp",EDGE,"E6.1.0"),sQuery(id+"F0.wireOp",EDGE,"E6.1.1"),subQ0,sQuery(id+"F0.wireOp",EDGE,"E6.1.3"),sQuery(id+"F0.wireOp",EDGE,"E6.1.4"),sQuery(id+"F0.wireOp",EDGE,"E6.1.5"),sQuery(id+"F0.wireOp",EDGE,"E6.1.6"),sQuery(id+"F0.wireOp",EDGE,"E6.1.7"),sQuery(id+"F0.wireOp",EDGE,"E6.1.8"),sQuery(id+"F0.wireOp",EDGE,"E6.2.0"),sQuery(id+"F0.wireOp",EDGE,"E6.2.1"),sQuery(id+"F0.wireOp",EDGE,"E6.2.2"),sQuery(id+"F0.wireOp",EDGE,"E6.2.3"),sQuery(id+"F0.wireOp",EDGE,"E6.2.4"),sQuery(id+"F0.wireOp",EDGE,"E6.2.5"),sQuery(id+"F0.wireOp",EDGE,"E6.2.6"),sQuery(id+"F0.wireOp",EDGE,"E6.2.7"),sQuery(id+"F0.wireOp",EDGE,"E6.2.8"),sQuery(id+"F0.wireOp",EDGE,"E6.3.0"),sQuery(id+"F0.wireOp",EDGE,"E6.3.1"),sQuery(id+"F0.wireOp",EDGE,"E6.3.2"),sQuery(id+"F0.wireOp",EDGE,"E6.3.3"),sQuery(id+"F0.wireOp",EDGE,"E6.3.4"),sQuery(id+"F0.wireOp",EDGE,"E6.3.5"),sQuery(id+"F0.wireOp",EDGE,"E6.3.6"),sQuery(id+"F0.wireOp",EDGE,"E6.3.7"),sQuery(id+"F0.wireOp",EDGE,"E6.3.8"),sQuery(id+"F0.wireOp",EDGE,"E6.4.0"),sQuery(id+"F0.wireOp",EDGE,"E6.4.1"),sQuery(id+"F0.wireOp",EDGE,"E6.4.2"),sQuery(id+"F0.wireOp",EDGE,"E6.4.3"),sQuery(id+"F0.wireOp",EDGE,"E6.4.4"),sQuery(id+"F0.wireOp",EDGE,"E6.4.5"),sQuery(id+"F0.wireOp",EDGE,"E6.4.6"),sQuery(id+"F0.wireOp",EDGE,"E6.4.7"),sQuery(id+"F0.wireOp",EDGE,"E6.4.8"),sQuery(id+"F0.wireOp",EDGE,"E6.5.0"),sQuery(id+"F0.wireOp",EDGE,"E6.5.1"),sQuery(id+"F0.wireOp",EDGE,"E6.5.2"),sQuery(id+"F0.wireOp",EDGE,"E6.5.3"),sQuery(id+"F0.wireOp",EDGE,"E6.5.4"),sQuery(id+"F0.wireOp",EDGE,"E6.5.5"),sQuery(id+"F0.wireOp",EDGE,"E6.5.6"),sQuery(id+"F0.wireOp",EDGE,"E6.5.7"),sQuery(id+"F0.wireOp",EDGE,"E6.5.8")])],"isStart":false})]});}
            var Q17;
            {var subQ0=sQuery(id+"F0.wireOp",EDGE,"E6.2.2");var subQ1=sQuery(id+"F0.wireOp",EDGE,"E6.1.0");Q17=makeQuery(id+"F2.opFillet","BLEND_EDGE",EDGE,{"blendedFrom":[makeQuery(id+"F1.opExtrude","SWEPT_EDGE",EDGE,{"disambiguationData":[OSD([subQ1,subQ0])]}),makeQuery(id+"F1.opExtrude","CAP_FACE",FACE,{"disambiguationData":[OSD([sQuery(id+"F0.wireOp",EDGE,"E0"),sQuery(id+"F0.wireOp",EDGE,"E1.0"),sQuery(id+"F0.wireOp",EDGE,"E1.1"),sQuery(id+"F0.wireOp",EDGE,"E1.2"),sQuery(id+"F0.wireOp",EDGE,"E1.3"),sQuery(id+"F0.wireOp",EDGE,"E1.4"),sQuery(id+"F0.wireOp",EDGE,"E1.5"),sQuery(id+"F0.wireOp",EDGE,"E2"),sQuery(id+"F0.wireOp",EDGE,"E3"),sQuery(id+"F0.wireOp",EDGE,"E4"),subQ1,sQuery(id+"F0.wireOp",EDGE,"E6.1.1"),sQuery(id+"F0.wireOp",EDGE,"E6.1.2"),sQuery(id+"F0.wireOp",EDGE,"E6.1.3"),sQuery(id+"F0.wireOp",EDGE,"E6.1.4"),sQuery(id+"F0.wireOp",EDGE,"E6.1.5"),sQuery(id+"F0.wireOp",EDGE,"E6.1.6"),sQuery(id+"F0.wireOp",EDGE,"E6.1.7"),sQuery(id+"F0.wireOp",EDGE,"E6.1.8"),sQuery(id+"F0.wireOp",EDGE,"E6.2.0"),sQuery(id+"F0.wireOp",EDGE,"E6.2.1"),subQ0,sQuery(id+"F0.wireOp",EDGE,"E6.2.3"),sQuery(id+"F0.wireOp",EDGE,"E6.2.4"),sQuery(id+"F0.wireOp",EDGE,"E6.2.5"),sQuery(id+"F0.wireOp",EDGE,"E6.2.6"),sQuery(id+"F0.wireOp",EDGE,"E6.2.7"),sQuery(id+"F0.wireOp",EDGE,"E6.2.8"),sQuery(id+"F0.wireOp",EDGE,"E6.3.0"),sQuery(id+"F0.wireOp",EDGE,"E6.3.1"),sQuery(id+"F0.wireOp",EDGE,"E6.3.2"),sQuery(id+"F0.wireOp",EDGE,"E6.3.3"),sQuery(id+"F0.wireOp",EDGE,"E6.3.4"),sQuery(id+"F0.wireOp",EDGE,"E6.3.5"),sQuery(id+"F0.wireOp",EDGE,"E6.3.6"),sQuery(id+"F0.wireOp",EDGE,"E6.3.7"),sQuery(id+"F0.wireOp",EDGE,"E6.3.8"),sQuery(id+"F0.wireOp",EDGE,"E6.4.0"),sQuery(id+"F0.wireOp",EDGE,"E6.4.1"),sQuery(id+"F0.wireOp",EDGE,"E6.4.2"),sQuery(id+"F0.wireOp",EDGE,"E6.4.3"),sQuery(id+"F0.wireOp",EDGE,"E6.4.4"),sQuery(id+"F0.wireOp",EDGE,"E6.4.5"),sQuery(id+"F0.wireOp",EDGE,"E6.4.6"),sQuery(id+"F0.wireOp",EDGE,"E6.4.7"),sQuery(id+"F0.wireOp",EDGE,"E6.4.8"),sQuery(id+"F0.wireOp",EDGE,"E6.5.0"),sQuery(id+"F0.wireOp",EDGE,"E6.5.1"),sQuery(id+"F0.wireOp",EDGE,"E6.5.2"),sQuery(id+"F0.wireOp",EDGE,"E6.5.3"),sQuery(id+"F0.wireOp",EDGE,"E6.5.4"),sQuery(id+"F0.wireOp",EDGE,"E6.5.5"),sQuery(id+"F0.wireOp",EDGE,"E6.5.6"),sQuery(id+"F0.wireOp",EDGE,"E6.5.7"),sQuery(id+"F0.wireOp",EDGE,"E6.5.8")])],"isStart":false})],"blendedInto":[makeQuery(id+"F1.opExtrude","CAP_FACE",FACE,{"disambiguationData":[OSD([sQuery(id+"F0.wireOp",EDGE,"E0"),sQuery(id+"F0.wireOp",EDGE,"E1.0"),sQuery(id+"F0.wireOp",EDGE,"E1.1"),sQuery(id+"F0.wireOp",EDGE,"E1.2"),sQuery(id+"F0.wireOp",EDGE,"E1.3"),sQuery(id+"F0.wireOp",EDGE,"E1.4"),sQuery(id+"F0.wireOp",EDGE,"E1.5"),sQuery(id+"F0.wireOp",EDGE,"E2"),sQuery(id+"F0.wireOp",EDGE,"E3"),sQuery(id+"F0.wireOp",EDGE,"E4"),subQ1,sQuery(id+"F0.wireOp",EDGE,"E6.1.1"),sQuery(id+"F0.wireOp",EDGE,"E6.1.2"),sQuery(id+"F0.wireOp",EDGE,"E6.1.3"),sQuery(id+"F0.wireOp",EDGE,"E6.1.4"),sQuery(id+"F0.wireOp",EDGE,"E6.1.5"),sQuery(id+"F0.wireOp",EDGE,"E6.1.6"),sQuery(id+"F0.wireOp",EDGE,"E6.1.7"),sQuery(id+"F0.wireOp",EDGE,"E6.1.8"),sQuery(id+"F0.wireOp",EDGE,"E6.2.0"),sQuery(id+"F0.wireOp",EDGE,"E6.2.1"),subQ0,sQuery(id+"F0.wireOp",EDGE,"E6.2.3"),sQuery(id+"F0.wireOp",EDGE,"E6.2.4"),sQuery(id+"F0.wireOp",EDGE,"E6.2.5"),sQuery(id+"F0.wireOp",EDGE,"E6.2.6"),sQuery(id+"F0.wireOp",EDGE,"E6.2.7"),sQuery(id+"F0.wireOp",EDGE,"E6.2.8"),sQuery(id+"F0.wireOp",EDGE,"E6.3.0"),sQuery(id+"F0.wireOp",EDGE,"E6.3.1"),sQuery(id+"F0.wireOp",EDGE,"E6.3.2"),sQuery(id+"F0.wireOp",EDGE,"E6.3.3"),sQuery(id+"F0.wireOp",EDGE,"E6.3.4"),sQuery(id+"F0.wireOp",EDGE,"E6.3.5"),sQuery(id+"F0.wireOp",EDGE,"E6.3.6"),sQuery(id+"F0.wireOp",EDGE,"E6.3.7"),sQuery(id+"F0.wireOp",EDGE,"E6.3.8"),sQuery(id+"F0.wireOp",EDGE,"E6.4.0"),sQuery(id+"F0.wireOp",EDGE,"E6.4.1"),sQuery(id+"F0.wireOp",EDGE,"E6.4.2"),sQuery(id+"F0.wireOp",EDGE,"E6.4.3"),sQuery(id+"F0.wireOp",EDGE,"E6.4.4"),sQuery(id+"F0.wireOp",EDGE,"E6.4.5"),sQuery(id+"F0.wireOp",EDGE,"E6.4.6"),sQuery(id+"F0.wireOp",EDGE,"E6.4.7"),sQuery(id+"F0.wireOp",EDGE,"E6.4.8"),sQuery(id+"F0.wireOp",EDGE,"E6.5.0"),sQuery(id+"F0.wireOp",EDGE,"E6.5.1"),sQuery(id+"F0.wireOp",EDGE,"E6.5.2"),sQuery(id+"F0.wireOp",EDGE,"E6.5.3"),sQuery(id+"F0.wireOp",EDGE,"E6.5.4"),sQuery(id+"F0.wireOp",EDGE,"E6.5.5"),sQuery(id+"F0.wireOp",EDGE,"E6.5.6"),sQuery(id+"F0.wireOp",EDGE,"E6.5.7"),sQuery(id+"F0.wireOp",EDGE,"E6.5.8")])],"isStart":false})]});}
            var Q18;
            {var subQ0=sQuery(id+"F0.wireOp",EDGE,"E6.3.2");var subQ1=sQuery(id+"F0.wireOp",EDGE,"E6.2.0");Q18=makeQuery(id+"F2.opFillet","BLEND_EDGE",EDGE,{"blendedFrom":[makeQuery(id+"F1.opExtrude","SWEPT_EDGE",EDGE,{"disambiguationData":[OSD([subQ1,subQ0])]}),makeQuery(id+"F1.opExtrude","CAP_FACE",FACE,{"disambiguationData":[OSD([sQuery(id+"F0.wireOp",EDGE,"E0"),sQuery(id+"F0.wireOp",EDGE,"E1.0"),sQuery(id+"F0.wireOp",EDGE,"E1.1"),sQuery(id+"F0.wireOp",EDGE,"E1.2"),sQuery(id+"F0.wireOp",EDGE,"E1.3"),sQuery(id+"F0.wireOp",EDGE,"E1.4"),sQuery(id+"F0.wireOp",EDGE,"E1.5"),sQuery(id+"F0.wireOp",EDGE,"E2"),sQuery(id+"F0.wireOp",EDGE,"E3"),sQuery(id+"F0.wireOp",EDGE,"E4"),sQuery(id+"F0.wireOp",EDGE,"E6.1.0"),sQuery(id+"F0.wireOp",EDGE,"E6.1.1"),sQuery(id+"F0.wireOp",EDGE,"E6.1.2"),sQuery(id+"F0.wireOp",EDGE,"E6.1.3"),sQuery(id+"F0.wireOp",EDGE,"E6.1.4"),sQuery(id+"F0.wireOp",EDGE,"E6.1.5"),sQuery(id+"F0.wireOp",EDGE,"E6.1.6"),sQuery(id+"F0.wireOp",EDGE,"E6.1.7"),sQuery(id+"F0.wireOp",EDGE,"E6.1.8"),subQ1,sQuery(id+"F0.wireOp",EDGE,"E6.2.1"),sQuery(id+"F0.wireOp",EDGE,"E6.2.2"),sQuery(id+"F0.wireOp",EDGE,"E6.2.3"),sQuery(id+"F0.wireOp",EDGE,"E6.2.4"),sQuery(id+"F0.wireOp",EDGE,"E6.2.5"),sQuery(id+"F0.wireOp",EDGE,"E6.2.6"),sQuery(id+"F0.wireOp",EDGE,"E6.2.7"),sQuery(id+"F0.wireOp",EDGE,"E6.2.8"),sQuery(id+"F0.wireOp",EDGE,"E6.3.0"),sQuery(id+"F0.wireOp",EDGE,"E6.3.1"),subQ0,sQuery(id+"F0.wireOp",EDGE,"E6.3.3"),sQuery(id+"F0.wireOp",EDGE,"E6.3.4"),sQuery(id+"F0.wireOp",EDGE,"E6.3.5"),sQuery(id+"F0.wireOp",EDGE,"E6.3.6"),sQuery(id+"F0.wireOp",EDGE,"E6.3.7"),sQuery(id+"F0.wireOp",EDGE,"E6.3.8"),sQuery(id+"F0.wireOp",EDGE,"E6.4.0"),sQuery(id+"F0.wireOp",EDGE,"E6.4.1"),sQuery(id+"F0.wireOp",EDGE,"E6.4.2"),sQuery(id+"F0.wireOp",EDGE,"E6.4.3"),sQuery(id+"F0.wireOp",EDGE,"E6.4.4"),sQuery(id+"F0.wireOp",EDGE,"E6.4.5"),sQuery(id+"F0.wireOp",EDGE,"E6.4.6"),sQuery(id+"F0.wireOp",EDGE,"E6.4.7"),sQuery(id+"F0.wireOp",EDGE,"E6.4.8"),sQuery(id+"F0.wireOp",EDGE,"E6.5.0"),sQuery(id+"F0.wireOp",EDGE,"E6.5.1"),sQuery(id+"F0.wireOp",EDGE,"E6.5.2"),sQuery(id+"F0.wireOp",EDGE,"E6.5.3"),sQuery(id+"F0.wireOp",EDGE,"E6.5.4"),sQuery(id+"F0.wireOp",EDGE,"E6.5.5"),sQuery(id+"F0.wireOp",EDGE,"E6.5.6"),sQuery(id+"F0.wireOp",EDGE,"E6.5.7"),sQuery(id+"F0.wireOp",EDGE,"E6.5.8")])],"isStart":true})],"blendedInto":[makeQuery(id+"F1.opExtrude","CAP_FACE",FACE,{"disambiguationData":[OSD([sQuery(id+"F0.wireOp",EDGE,"E0"),sQuery(id+"F0.wireOp",EDGE,"E1.0"),sQuery(id+"F0.wireOp",EDGE,"E1.1"),sQuery(id+"F0.wireOp",EDGE,"E1.2"),sQuery(id+"F0.wireOp",EDGE,"E1.3"),sQuery(id+"F0.wireOp",EDGE,"E1.4"),sQuery(id+"F0.wireOp",EDGE,"E1.5"),sQuery(id+"F0.wireOp",EDGE,"E2"),sQuery(id+"F0.wireOp",EDGE,"E3"),sQuery(id+"F0.wireOp",EDGE,"E4"),sQuery(id+"F0.wireOp",EDGE,"E6.1.0"),sQuery(id+"F0.wireOp",EDGE,"E6.1.1"),sQuery(id+"F0.wireOp",EDGE,"E6.1.2"),sQuery(id+"F0.wireOp",EDGE,"E6.1.3"),sQuery(id+"F0.wireOp",EDGE,"E6.1.4"),sQuery(id+"F0.wireOp",EDGE,"E6.1.5"),sQuery(id+"F0.wireOp",EDGE,"E6.1.6"),sQuery(id+"F0.wireOp",EDGE,"E6.1.7"),sQuery(id+"F0.wireOp",EDGE,"E6.1.8"),subQ1,sQuery(id+"F0.wireOp",EDGE,"E6.2.1"),sQuery(id+"F0.wireOp",EDGE,"E6.2.2"),sQuery(id+"F0.wireOp",EDGE,"E6.2.3"),sQuery(id+"F0.wireOp",EDGE,"E6.2.4"),sQuery(id+"F0.wireOp",EDGE,"E6.2.5"),sQuery(id+"F0.wireOp",EDGE,"E6.2.6"),sQuery(id+"F0.wireOp",EDGE,"E6.2.7"),sQuery(id+"F0.wireOp",EDGE,"E6.2.8"),sQuery(id+"F0.wireOp",EDGE,"E6.3.0"),sQuery(id+"F0.wireOp",EDGE,"E6.3.1"),subQ0,sQuery(id+"F0.wireOp",EDGE,"E6.3.3"),sQuery(id+"F0.wireOp",EDGE,"E6.3.4"),sQuery(id+"F0.wireOp",EDGE,"E6.3.5"),sQuery(id+"F0.wireOp",EDGE,"E6.3.6"),sQuery(id+"F0.wireOp",EDGE,"E6.3.7"),sQuery(id+"F0.wireOp",EDGE,"E6.3.8"),sQuery(id+"F0.wireOp",EDGE,"E6.4.0"),sQuery(id+"F0.wireOp",EDGE,"E6.4.1"),sQuery(id+"F0.wireOp",EDGE,"E6.4.2"),sQuery(id+"F0.wireOp",EDGE,"E6.4.3"),sQuery(id+"F0.wireOp",EDGE,"E6.4.4"),sQuery(id+"F0.wireOp",EDGE,"E6.4.5"),sQuery(id+"F0.wireOp",EDGE,"E6.4.6"),sQuery(id+"F0.wireOp",EDGE,"E6.4.7"),sQuery(id+"F0.wireOp",EDGE,"E6.4.8"),sQuery(id+"F0.wireOp",EDGE,"E6.5.0"),sQuery(id+"F0.wireOp",EDGE,"E6.5.1"),sQuery(id+"F0.wireOp",EDGE,"E6.5.2"),sQuery(id+"F0.wireOp",EDGE,"E6.5.3"),sQuery(id+"F0.wireOp",EDGE,"E6.5.4"),sQuery(id+"F0.wireOp",EDGE,"E6.5.5"),sQuery(id+"F0.wireOp",EDGE,"E6.5.6"),sQuery(id+"F0.wireOp",EDGE,"E6.5.7"),sQuery(id+"F0.wireOp",EDGE,"E6.5.8")])],"isStart":true})]});}
            var Q19;
            {var subQ0=sQuery(id+"F0.wireOp",EDGE,"E6.2.2");var subQ1=sQuery(id+"F0.wireOp",EDGE,"E6.1.0");Q19=makeQuery(id+"F2.opFillet","BLEND_EDGE",EDGE,{"blendedFrom":[makeQuery(id+"F1.opExtrude","SWEPT_EDGE",EDGE,{"disambiguationData":[OSD([subQ1,subQ0])]}),makeQuery(id+"F1.opExtrude","CAP_FACE",FACE,{"disambiguationData":[OSD([sQuery(id+"F0.wireOp",EDGE,"E0"),sQuery(id+"F0.wireOp",EDGE,"E1.0"),sQuery(id+"F0.wireOp",EDGE,"E1.1"),sQuery(id+"F0.wireOp",EDGE,"E1.2"),sQuery(id+"F0.wireOp",EDGE,"E1.3"),sQuery(id+"F0.wireOp",EDGE,"E1.4"),sQuery(id+"F0.wireOp",EDGE,"E1.5"),sQuery(id+"F0.wireOp",EDGE,"E2"),sQuery(id+"F0.wireOp",EDGE,"E3"),sQuery(id+"F0.wireOp",EDGE,"E4"),subQ1,sQuery(id+"F0.wireOp",EDGE,"E6.1.1"),sQuery(id+"F0.wireOp",EDGE,"E6.1.2"),sQuery(id+"F0.wireOp",EDGE,"E6.1.3"),sQuery(id+"F0.wireOp",EDGE,"E6.1.4"),sQuery(id+"F0.wireOp",EDGE,"E6.1.5"),sQuery(id+"F0.wireOp",EDGE,"E6.1.6"),sQuery(id+"F0.wireOp",EDGE,"E6.1.7"),sQuery(id+"F0.wireOp",EDGE,"E6.1.8"),sQuery(id+"F0.wireOp",EDGE,"E6.2.0"),sQuery(id+"F0.wireOp",EDGE,"E6.2.1"),subQ0,sQuery(id+"F0.wireOp",EDGE,"E6.2.3"),sQuery(id+"F0.wireOp",EDGE,"E6.2.4"),sQuery(id+"F0.wireOp",EDGE,"E6.2.5"),sQuery(id+"F0.wireOp",EDGE,"E6.2.6"),sQuery(id+"F0.wireOp",EDGE,"E6.2.7"),sQuery(id+"F0.wireOp",EDGE,"E6.2.8"),sQuery(id+"F0.wireOp",EDGE,"E6.3.0"),sQuery(id+"F0.wireOp",EDGE,"E6.3.1"),sQuery(id+"F0.wireOp",EDGE,"E6.3.2"),sQuery(id+"F0.wireOp",EDGE,"E6.3.3"),sQuery(id+"F0.wireOp",EDGE,"E6.3.4"),sQuery(id+"F0.wireOp",EDGE,"E6.3.5"),sQuery(id+"F0.wireOp",EDGE,"E6.3.6"),sQuery(id+"F0.wireOp",EDGE,"E6.3.7"),sQuery(id+"F0.wireOp",EDGE,"E6.3.8"),sQuery(id+"F0.wireOp",EDGE,"E6.4.0"),sQuery(id+"F0.wireOp",EDGE,"E6.4.1"),sQuery(id+"F0.wireOp",EDGE,"E6.4.2"),sQuery(id+"F0.wireOp",EDGE,"E6.4.3"),sQuery(id+"F0.wireOp",EDGE,"E6.4.4"),sQuery(id+"F0.wireOp",EDGE,"E6.4.5"),sQuery(id+"F0.wireOp",EDGE,"E6.4.6"),sQuery(id+"F0.wireOp",EDGE,"E6.4.7"),sQuery(id+"F0.wireOp",EDGE,"E6.4.8"),sQuery(id+"F0.wireOp",EDGE,"E6.5.0"),sQuery(id+"F0.wireOp",EDGE,"E6.5.1"),sQuery(id+"F0.wireOp",EDGE,"E6.5.2"),sQuery(id+"F0.wireOp",EDGE,"E6.5.3"),sQuery(id+"F0.wireOp",EDGE,"E6.5.4"),sQuery(id+"F0.wireOp",EDGE,"E6.5.5"),sQuery(id+"F0.wireOp",EDGE,"E6.5.6"),sQuery(id+"F0.wireOp",EDGE,"E6.5.7"),sQuery(id+"F0.wireOp",EDGE,"E6.5.8")])],"isStart":true})],"blendedInto":[makeQuery(id+"F1.opExtrude","CAP_FACE",FACE,{"disambiguationData":[OSD([sQuery(id+"F0.wireOp",EDGE,"E0"),sQuery(id+"F0.wireOp",EDGE,"E1.0"),sQuery(id+"F0.wireOp",EDGE,"E1.1"),sQuery(id+"F0.wireOp",EDGE,"E1.2"),sQuery(id+"F0.wireOp",EDGE,"E1.3"),sQuery(id+"F0.wireOp",EDGE,"E1.4"),sQuery(id+"F0.wireOp",EDGE,"E1.5"),sQuery(id+"F0.wireOp",EDGE,"E2"),sQuery(id+"F0.wireOp",EDGE,"E3"),sQuery(id+"F0.wireOp",EDGE,"E4"),subQ1,sQuery(id+"F0.wireOp",EDGE,"E6.1.1"),sQuery(id+"F0.wireOp",EDGE,"E6.1.2"),sQuery(id+"F0.wireOp",EDGE,"E6.1.3"),sQuery(id+"F0.wireOp",EDGE,"E6.1.4"),sQuery(id+"F0.wireOp",EDGE,"E6.1.5"),sQuery(id+"F0.wireOp",EDGE,"E6.1.6"),sQuery(id+"F0.wireOp",EDGE,"E6.1.7"),sQuery(id+"F0.wireOp",EDGE,"E6.1.8"),sQuery(id+"F0.wireOp",EDGE,"E6.2.0"),sQuery(id+"F0.wireOp",EDGE,"E6.2.1"),subQ0,sQuery(id+"F0.wireOp",EDGE,"E6.2.3"),sQuery(id+"F0.wireOp",EDGE,"E6.2.4"),sQuery(id+"F0.wireOp",EDGE,"E6.2.5"),sQuery(id+"F0.wireOp",EDGE,"E6.2.6"),sQuery(id+"F0.wireOp",EDGE,"E6.2.7"),sQuery(id+"F0.wireOp",EDGE,"E6.2.8"),sQuery(id+"F0.wireOp",EDGE,"E6.3.0"),sQuery(id+"F0.wireOp",EDGE,"E6.3.1"),sQuery(id+"F0.wireOp",EDGE,"E6.3.2"),sQuery(id+"F0.wireOp",EDGE,"E6.3.3"),sQuery(id+"F0.wireOp",EDGE,"E6.3.4"),sQuery(id+"F0.wireOp",EDGE,"E6.3.5"),sQuery(id+"F0.wireOp",EDGE,"E6.3.6"),sQuery(id+"F0.wireOp",EDGE,"E6.3.7"),sQuery(id+"F0.wireOp",EDGE,"E6.3.8"),sQuery(id+"F0.wireOp",EDGE,"E6.4.0"),sQuery(id+"F0.wireOp",EDGE,"E6.4.1"),sQuery(id+"F0.wireOp",EDGE,"E6.4.2"),sQuery(id+"F0.wireOp",EDGE,"E6.4.3"),sQuery(id+"F0.wireOp",EDGE,"E6.4.4"),sQuery(id+"F0.wireOp",EDGE,"E6.4.5"),sQuery(id+"F0.wireOp",EDGE,"E6.4.6"),sQuery(id+"F0.wireOp",EDGE,"E6.4.7"),sQuery(id+"F0.wireOp",EDGE,"E6.4.8"),sQuery(id+"F0.wireOp",EDGE,"E6.5.0"),sQuery(id+"F0.wireOp",EDGE,"E6.5.1"),sQuery(id+"F0.wireOp",EDGE,"E6.5.2"),sQuery(id+"F0.wireOp",EDGE,"E6.5.3"),sQuery(id+"F0.wireOp",EDGE,"E6.5.4"),sQuery(id+"F0.wireOp",EDGE,"E6.5.5"),sQuery(id+"F0.wireOp",EDGE,"E6.5.6"),sQuery(id+"F0.wireOp",EDGE,"E6.5.7"),sQuery(id+"F0.wireOp",EDGE,"E6.5.8")])],"isStart":true})]});}
            var Q20;
            {var subQ0=sQuery(id+"F0.wireOp",EDGE,"E6.1.2");var subQ1=sQuery(id+"F0.wireOp",EDGE,"E3");Q20=makeQuery(id+"F2.opFillet","BLEND_EDGE",EDGE,{"blendedFrom":[makeQuery(id+"F1.opExtrude","SWEPT_EDGE",EDGE,{"disambiguationData":[OSD([subQ1,subQ0])]}),makeQuery(id+"F1.opExtrude","CAP_FACE",FACE,{"disambiguationData":[OSD([sQuery(id+"F0.wireOp",EDGE,"E0"),sQuery(id+"F0.wireOp",EDGE,"E1.0"),sQuery(id+"F0.wireOp",EDGE,"E1.1"),sQuery(id+"F0.wireOp",EDGE,"E1.2"),sQuery(id+"F0.wireOp",EDGE,"E1.3"),sQuery(id+"F0.wireOp",EDGE,"E1.4"),sQuery(id+"F0.wireOp",EDGE,"E1.5"),sQuery(id+"F0.wireOp",EDGE,"E2"),subQ1,sQuery(id+"F0.wireOp",EDGE,"E4"),sQuery(id+"F0.wireOp",EDGE,"E6.1.0"),sQuery(id+"F0.wireOp",EDGE,"E6.1.1"),subQ0,sQuery(id+"F0.wireOp",EDGE,"E6.1.3"),sQuery(id+"F0.wireOp",EDGE,"E6.1.4"),sQuery(id+"F0.wireOp",EDGE,"E6.1.5"),sQuery(id+"F0.wireOp",EDGE,"E6.1.6"),sQuery(id+"F0.wireOp",EDGE,"E6.1.7"),sQuery(id+"F0.wireOp",EDGE,"E6.1.8"),sQuery(id+"F0.wireOp",EDGE,"E6.2.0"),sQuery(id+"F0.wireOp",EDGE,"E6.2.1"),sQuery(id+"F0.wireOp",EDGE,"E6.2.2"),sQuery(id+"F0.wireOp",EDGE,"E6.2.3"),sQuery(id+"F0.wireOp",EDGE,"E6.2.4"),sQuery(id+"F0.wireOp",EDGE,"E6.2.5"),sQuery(id+"F0.wireOp",EDGE,"E6.2.6"),sQuery(id+"F0.wireOp",EDGE,"E6.2.7"),sQuery(id+"F0.wireOp",EDGE,"E6.2.8"),sQuery(id+"F0.wireOp",EDGE,"E6.3.0"),sQuery(id+"F0.wireOp",EDGE,"E6.3.1"),sQuery(id+"F0.wireOp",EDGE,"E6.3.2"),sQuery(id+"F0.wireOp",EDGE,"E6.3.3"),sQuery(id+"F0.wireOp",EDGE,"E6.3.4"),sQuery(id+"F0.wireOp",EDGE,"E6.3.5"),sQuery(id+"F0.wireOp",EDGE,"E6.3.6"),sQuery(id+"F0.wireOp",EDGE,"E6.3.7"),sQuery(id+"F0.wireOp",EDGE,"E6.3.8"),sQuery(id+"F0.wireOp",EDGE,"E6.4.0"),sQuery(id+"F0.wireOp",EDGE,"E6.4.1"),sQuery(id+"F0.wireOp",EDGE,"E6.4.2"),sQuery(id+"F0.wireOp",EDGE,"E6.4.3"),sQuery(id+"F0.wireOp",EDGE,"E6.4.4"),sQuery(id+"F0.wireOp",EDGE,"E6.4.5"),sQuery(id+"F0.wireOp",EDGE,"E6.4.6"),sQuery(id+"F0.wireOp",EDGE,"E6.4.7"),sQuery(id+"F0.wireOp",EDGE,"E6.4.8"),sQuery(id+"F0.wireOp",EDGE,"E6.5.0"),sQuery(id+"F0.wireOp",EDGE,"E6.5.1"),sQuery(id+"F0.wireOp",EDGE,"E6.5.2"),sQuery(id+"F0.wireOp",EDGE,"E6.5.3"),sQuery(id+"F0.wireOp",EDGE,"E6.5.4"),sQuery(id+"F0.wireOp",EDGE,"E6.5.5"),sQuery(id+"F0.wireOp",EDGE,"E6.5.6"),sQuery(id+"F0.wireOp",EDGE,"E6.5.7"),sQuery(id+"F0.wireOp",EDGE,"E6.5.8")])],"isStart":true})],"blendedInto":[makeQuery(id+"F1.opExtrude","CAP_FACE",FACE,{"disambiguationData":[OSD([sQuery(id+"F0.wireOp",EDGE,"E0"),sQuery(id+"F0.wireOp",EDGE,"E1.0"),sQuery(id+"F0.wireOp",EDGE,"E1.1"),sQuery(id+"F0.wireOp",EDGE,"E1.2"),sQuery(id+"F0.wireOp",EDGE,"E1.3"),sQuery(id+"F0.wireOp",EDGE,"E1.4"),sQuery(id+"F0.wireOp",EDGE,"E1.5"),sQuery(id+"F0.wireOp",EDGE,"E2"),subQ1,sQuery(id+"F0.wireOp",EDGE,"E4"),sQuery(id+"F0.wireOp",EDGE,"E6.1.0"),sQuery(id+"F0.wireOp",EDGE,"E6.1.1"),subQ0,sQuery(id+"F0.wireOp",EDGE,"E6.1.3"),sQuery(id+"F0.wireOp",EDGE,"E6.1.4"),sQuery(id+"F0.wireOp",EDGE,"E6.1.5"),sQuery(id+"F0.wireOp",EDGE,"E6.1.6"),sQuery(id+"F0.wireOp",EDGE,"E6.1.7"),sQuery(id+"F0.wireOp",EDGE,"E6.1.8"),sQuery(id+"F0.wireOp",EDGE,"E6.2.0"),sQuery(id+"F0.wireOp",EDGE,"E6.2.1"),sQuery(id+"F0.wireOp",EDGE,"E6.2.2"),sQuery(id+"F0.wireOp",EDGE,"E6.2.3"),sQuery(id+"F0.wireOp",EDGE,"E6.2.4"),sQuery(id+"F0.wireOp",EDGE,"E6.2.5"),sQuery(id+"F0.wireOp",EDGE,"E6.2.6"),sQuery(id+"F0.wireOp",EDGE,"E6.2.7"),sQuery(id+"F0.wireOp",EDGE,"E6.2.8"),sQuery(id+"F0.wireOp",EDGE,"E6.3.0"),sQuery(id+"F0.wireOp",EDGE,"E6.3.1"),sQuery(id+"F0.wireOp",EDGE,"E6.3.2"),sQuery(id+"F0.wireOp",EDGE,"E6.3.3"),sQuery(id+"F0.wireOp",EDGE,"E6.3.4"),sQuery(id+"F0.wireOp",EDGE,"E6.3.5"),sQuery(id+"F0.wireOp",EDGE,"E6.3.6"),sQuery(id+"F0.wireOp",EDGE,"E6.3.7"),sQuery(id+"F0.wireOp",EDGE,"E6.3.8"),sQuery(id+"F0.wireOp",EDGE,"E6.4.0"),sQuery(id+"F0.wireOp",EDGE,"E6.4.1"),sQuery(id+"F0.wireOp",EDGE,"E6.4.2"),sQuery(id+"F0.wireOp",EDGE,"E6.4.3"),sQuery(id+"F0.wireOp",EDGE,"E6.4.4"),sQuery(id+"F0.wireOp",EDGE,"E6.4.5"),sQuery(id+"F0.wireOp",EDGE,"E6.4.6"),sQuery(id+"F0.wireOp",EDGE,"E6.4.7"),sQuery(id+"F0.wireOp",EDGE,"E6.4.8"),sQuery(id+"F0.wireOp",EDGE,"E6.5.0"),sQuery(id+"F0.wireOp",EDGE,"E6.5.1"),sQuery(id+"F0.wireOp",EDGE,"E6.5.2"),sQuery(id+"F0.wireOp",EDGE,"E6.5.3"),sQuery(id+"F0.wireOp",EDGE,"E6.5.4"),sQuery(id+"F0.wireOp",EDGE,"E6.5.5"),sQuery(id+"F0.wireOp",EDGE,"E6.5.6"),sQuery(id+"F0.wireOp",EDGE,"E6.5.7"),sQuery(id+"F0.wireOp",EDGE,"E6.5.8")])],"isStart":true})]});}
            var Q21;
            {var subQ0=sQuery(id+"F0.wireOp",EDGE,"E6.5.0");var subQ1=sQuery(id+"F0.wireOp",EDGE,"E4");Q21=makeQuery(id+"F2.opFillet","BLEND_EDGE",EDGE,{"blendedFrom":[makeQuery(id+"F1.opExtrude","SWEPT_EDGE",EDGE,{"disambiguationData":[OSD([subQ1,subQ0])]}),makeQuery(id+"F1.opExtrude","CAP_FACE",FACE,{"disambiguationData":[OSD([sQuery(id+"F0.wireOp",EDGE,"E0"),sQuery(id+"F0.wireOp",EDGE,"E1.0"),sQuery(id+"F0.wireOp",EDGE,"E1.1"),sQuery(id+"F0.wireOp",EDGE,"E1.2"),sQuery(id+"F0.wireOp",EDGE,"E1.3"),sQuery(id+"F0.wireOp",EDGE,"E1.4"),sQuery(id+"F0.wireOp",EDGE,"E1.5"),sQuery(id+"F0.wireOp",EDGE,"E2"),sQuery(id+"F0.wireOp",EDGE,"E3"),subQ1,sQuery(id+"F0.wireOp",EDGE,"E6.1.0"),sQuery(id+"F0.wireOp",EDGE,"E6.1.1"),sQuery(id+"F0.wireOp",EDGE,"E6.1.2"),sQuery(id+"F0.wireOp",EDGE,"E6.1.3"),sQuery(id+"F0.wireOp",EDGE,"E6.1.4"),sQuery(id+"F0.wireOp",EDGE,"E6.1.5"),sQuery(id+"F0.wireOp",EDGE,"E6.1.6"),sQuery(id+"F0.wireOp",EDGE,"E6.1.7"),sQuery(id+"F0.wireOp",EDGE,"E6.1.8"),sQuery(id+"F0.wireOp",EDGE,"E6.2.0"),sQuery(id+"F0.wireOp",EDGE,"E6.2.1"),sQuery(id+"F0.wireOp",EDGE,"E6.2.2"),sQuery(id+"F0.wireOp",EDGE,"E6.2.3"),sQuery(id+"F0.wireOp",EDGE,"E6.2.4"),sQuery(id+"F0.wireOp",EDGE,"E6.2.5"),sQuery(id+"F0.wireOp",EDGE,"E6.2.6"),sQuery(id+"F0.wireOp",EDGE,"E6.2.7"),sQuery(id+"F0.wireOp",EDGE,"E6.2.8"),sQuery(id+"F0.wireOp",EDGE,"E6.3.0"),sQuery(id+"F0.wireOp",EDGE,"E6.3.1"),sQuery(id+"F0.wireOp",EDGE,"E6.3.2"),sQuery(id+"F0.wireOp",EDGE,"E6.3.3"),sQuery(id+"F0.wireOp",EDGE,"E6.3.4"),sQuery(id+"F0.wireOp",EDGE,"E6.3.5"),sQuery(id+"F0.wireOp",EDGE,"E6.3.6"),sQuery(id+"F0.wireOp",EDGE,"E6.3.7"),sQuery(id+"F0.wireOp",EDGE,"E6.3.8"),sQuery(id+"F0.wireOp",EDGE,"E6.4.0"),sQuery(id+"F0.wireOp",EDGE,"E6.4.1"),sQuery(id+"F0.wireOp",EDGE,"E6.4.2"),sQuery(id+"F0.wireOp",EDGE,"E6.4.3"),sQuery(id+"F0.wireOp",EDGE,"E6.4.4"),sQuery(id+"F0.wireOp",EDGE,"E6.4.5"),sQuery(id+"F0.wireOp",EDGE,"E6.4.6"),sQuery(id+"F0.wireOp",EDGE,"E6.4.7"),sQuery(id+"F0.wireOp",EDGE,"E6.4.8"),subQ0,sQuery(id+"F0.wireOp",EDGE,"E6.5.1"),sQuery(id+"F0.wireOp",EDGE,"E6.5.2"),sQuery(id+"F0.wireOp",EDGE,"E6.5.3"),sQuery(id+"F0.wireOp",EDGE,"E6.5.4"),sQuery(id+"F0.wireOp",EDGE,"E6.5.5"),sQuery(id+"F0.wireOp",EDGE,"E6.5.6"),sQuery(id+"F0.wireOp",EDGE,"E6.5.7"),sQuery(id+"F0.wireOp",EDGE,"E6.5.8")])],"isStart":true})],"blendedInto":[makeQuery(id+"F1.opExtrude","CAP_FACE",FACE,{"disambiguationData":[OSD([sQuery(id+"F0.wireOp",EDGE,"E0"),sQuery(id+"F0.wireOp",EDGE,"E1.0"),sQuery(id+"F0.wireOp",EDGE,"E1.1"),sQuery(id+"F0.wireOp",EDGE,"E1.2"),sQuery(id+"F0.wireOp",EDGE,"E1.3"),sQuery(id+"F0.wireOp",EDGE,"E1.4"),sQuery(id+"F0.wireOp",EDGE,"E1.5"),sQuery(id+"F0.wireOp",EDGE,"E2"),sQuery(id+"F0.wireOp",EDGE,"E3"),subQ1,sQuery(id+"F0.wireOp",EDGE,"E6.1.0"),sQuery(id+"F0.wireOp",EDGE,"E6.1.1"),sQuery(id+"F0.wireOp",EDGE,"E6.1.2"),sQuery(id+"F0.wireOp",EDGE,"E6.1.3"),sQuery(id+"F0.wireOp",EDGE,"E6.1.4"),sQuery(id+"F0.wireOp",EDGE,"E6.1.5"),sQuery(id+"F0.wireOp",EDGE,"E6.1.6"),sQuery(id+"F0.wireOp",EDGE,"E6.1.7"),sQuery(id+"F0.wireOp",EDGE,"E6.1.8"),sQuery(id+"F0.wireOp",EDGE,"E6.2.0"),sQuery(id+"F0.wireOp",EDGE,"E6.2.1"),sQuery(id+"F0.wireOp",EDGE,"E6.2.2"),sQuery(id+"F0.wireOp",EDGE,"E6.2.3"),sQuery(id+"F0.wireOp",EDGE,"E6.2.4"),sQuery(id+"F0.wireOp",EDGE,"E6.2.5"),sQuery(id+"F0.wireOp",EDGE,"E6.2.6"),sQuery(id+"F0.wireOp",EDGE,"E6.2.7"),sQuery(id+"F0.wireOp",EDGE,"E6.2.8"),sQuery(id+"F0.wireOp",EDGE,"E6.3.0"),sQuery(id+"F0.wireOp",EDGE,"E6.3.1"),sQuery(id+"F0.wireOp",EDGE,"E6.3.2"),sQuery(id+"F0.wireOp",EDGE,"E6.3.3"),sQuery(id+"F0.wireOp",EDGE,"E6.3.4"),sQuery(id+"F0.wireOp",EDGE,"E6.3.5"),sQuery(id+"F0.wireOp",EDGE,"E6.3.6"),sQuery(id+"F0.wireOp",EDGE,"E6.3.7"),sQuery(id+"F0.wireOp",EDGE,"E6.3.8"),sQuery(id+"F0.wireOp",EDGE,"E6.4.0"),sQuery(id+"F0.wireOp",EDGE,"E6.4.1"),sQuery(id+"F0.wireOp",EDGE,"E6.4.2"),sQuery(id+"F0.wireOp",EDGE,"E6.4.3"),sQuery(id+"F0.wireOp",EDGE,"E6.4.4"),sQuery(id+"F0.wireOp",EDGE,"E6.4.5"),sQuery(id+"F0.wireOp",EDGE,"E6.4.6"),sQuery(id+"F0.wireOp",EDGE,"E6.4.7"),sQuery(id+"F0.wireOp",EDGE,"E6.4.8"),subQ0,sQuery(id+"F0.wireOp",EDGE,"E6.5.1"),sQuery(id+"F0.wireOp",EDGE,"E6.5.2"),sQuery(id+"F0.wireOp",EDGE,"E6.5.3"),sQuery(id+"F0.wireOp",EDGE,"E6.5.4"),sQuery(id+"F0.wireOp",EDGE,"E6.5.5"),sQuery(id+"F0.wireOp",EDGE,"E6.5.6"),sQuery(id+"F0.wireOp",EDGE,"E6.5.7"),sQuery(id+"F0.wireOp",EDGE,"E6.5.8")])],"isStart":true})]});}
            var Q22;
            {var subQ0=sQuery(id+"F0.wireOp",EDGE,"E6.5.2");var subQ1=sQuery(id+"F0.wireOp",EDGE,"E6.4.0");Q22=makeQuery(id+"F2.opFillet","BLEND_EDGE",EDGE,{"blendedFrom":[makeQuery(id+"F1.opExtrude","SWEPT_EDGE",EDGE,{"disambiguationData":[OSD([subQ1,subQ0])]}),makeQuery(id+"F1.opExtrude","CAP_FACE",FACE,{"disambiguationData":[OSD([sQuery(id+"F0.wireOp",EDGE,"E0"),sQuery(id+"F0.wireOp",EDGE,"E1.0"),sQuery(id+"F0.wireOp",EDGE,"E1.1"),sQuery(id+"F0.wireOp",EDGE,"E1.2"),sQuery(id+"F0.wireOp",EDGE,"E1.3"),sQuery(id+"F0.wireOp",EDGE,"E1.4"),sQuery(id+"F0.wireOp",EDGE,"E1.5"),sQuery(id+"F0.wireOp",EDGE,"E2"),sQuery(id+"F0.wireOp",EDGE,"E3"),sQuery(id+"F0.wireOp",EDGE,"E4"),sQuery(id+"F0.wireOp",EDGE,"E6.1.0"),sQuery(id+"F0.wireOp",EDGE,"E6.1.1"),sQuery(id+"F0.wireOp",EDGE,"E6.1.2"),sQuery(id+"F0.wireOp",EDGE,"E6.1.3"),sQuery(id+"F0.wireOp",EDGE,"E6.1.4"),sQuery(id+"F0.wireOp",EDGE,"E6.1.5"),sQuery(id+"F0.wireOp",EDGE,"E6.1.6"),sQuery(id+"F0.wireOp",EDGE,"E6.1.7"),sQuery(id+"F0.wireOp",EDGE,"E6.1.8"),sQuery(id+"F0.wireOp",EDGE,"E6.2.0"),sQuery(id+"F0.wireOp",EDGE,"E6.2.1"),sQuery(id+"F0.wireOp",EDGE,"E6.2.2"),sQuery(id+"F0.wireOp",EDGE,"E6.2.3"),sQuery(id+"F0.wireOp",EDGE,"E6.2.4"),sQuery(id+"F0.wireOp",EDGE,"E6.2.5"),sQuery(id+"F0.wireOp",EDGE,"E6.2.6"),sQuery(id+"F0.wireOp",EDGE,"E6.2.7"),sQuery(id+"F0.wireOp",EDGE,"E6.2.8"),sQuery(id+"F0.wireOp",EDGE,"E6.3.0"),sQuery(id+"F0.wireOp",EDGE,"E6.3.1"),sQuery(id+"F0.wireOp",EDGE,"E6.3.2"),sQuery(id+"F0.wireOp",EDGE,"E6.3.3"),sQuery(id+"F0.wireOp",EDGE,"E6.3.4"),sQuery(id+"F0.wireOp",EDGE,"E6.3.5"),sQuery(id+"F0.wireOp",EDGE,"E6.3.6"),sQuery(id+"F0.wireOp",EDGE,"E6.3.7"),sQuery(id+"F0.wireOp",EDGE,"E6.3.8"),subQ1,sQuery(id+"F0.wireOp",EDGE,"E6.4.1"),sQuery(id+"F0.wireOp",EDGE,"E6.4.2"),sQuery(id+"F0.wireOp",EDGE,"E6.4.3"),sQuery(id+"F0.wireOp",EDGE,"E6.4.4"),sQuery(id+"F0.wireOp",EDGE,"E6.4.5"),sQuery(id+"F0.wireOp",EDGE,"E6.4.6"),sQuery(id+"F0.wireOp",EDGE,"E6.4.7"),sQuery(id+"F0.wireOp",EDGE,"E6.4.8"),sQuery(id+"F0.wireOp",EDGE,"E6.5.0"),sQuery(id+"F0.wireOp",EDGE,"E6.5.1"),subQ0,sQuery(id+"F0.wireOp",EDGE,"E6.5.3"),sQuery(id+"F0.wireOp",EDGE,"E6.5.4"),sQuery(id+"F0.wireOp",EDGE,"E6.5.5"),sQuery(id+"F0.wireOp",EDGE,"E6.5.6"),sQuery(id+"F0.wireOp",EDGE,"E6.5.7"),sQuery(id+"F0.wireOp",EDGE,"E6.5.8")])],"isStart":true})],"blendedInto":[makeQuery(id+"F1.opExtrude","CAP_FACE",FACE,{"disambiguationData":[OSD([sQuery(id+"F0.wireOp",EDGE,"E0"),sQuery(id+"F0.wireOp",EDGE,"E1.0"),sQuery(id+"F0.wireOp",EDGE,"E1.1"),sQuery(id+"F0.wireOp",EDGE,"E1.2"),sQuery(id+"F0.wireOp",EDGE,"E1.3"),sQuery(id+"F0.wireOp",EDGE,"E1.4"),sQuery(id+"F0.wireOp",EDGE,"E1.5"),sQuery(id+"F0.wireOp",EDGE,"E2"),sQuery(id+"F0.wireOp",EDGE,"E3"),sQuery(id+"F0.wireOp",EDGE,"E4"),sQuery(id+"F0.wireOp",EDGE,"E6.1.0"),sQuery(id+"F0.wireOp",EDGE,"E6.1.1"),sQuery(id+"F0.wireOp",EDGE,"E6.1.2"),sQuery(id+"F0.wireOp",EDGE,"E6.1.3"),sQuery(id+"F0.wireOp",EDGE,"E6.1.4"),sQuery(id+"F0.wireOp",EDGE,"E6.1.5"),sQuery(id+"F0.wireOp",EDGE,"E6.1.6"),sQuery(id+"F0.wireOp",EDGE,"E6.1.7"),sQuery(id+"F0.wireOp",EDGE,"E6.1.8"),sQuery(id+"F0.wireOp",EDGE,"E6.2.0"),sQuery(id+"F0.wireOp",EDGE,"E6.2.1"),sQuery(id+"F0.wireOp",EDGE,"E6.2.2"),sQuery(id+"F0.wireOp",EDGE,"E6.2.3"),sQuery(id+"F0.wireOp",EDGE,"E6.2.4"),sQuery(id+"F0.wireOp",EDGE,"E6.2.5"),sQuery(id+"F0.wireOp",EDGE,"E6.2.6"),sQuery(id+"F0.wireOp",EDGE,"E6.2.7"),sQuery(id+"F0.wireOp",EDGE,"E6.2.8"),sQuery(id+"F0.wireOp",EDGE,"E6.3.0"),sQuery(id+"F0.wireOp",EDGE,"E6.3.1"),sQuery(id+"F0.wireOp",EDGE,"E6.3.2"),sQuery(id+"F0.wireOp",EDGE,"E6.3.3"),sQuery(id+"F0.wireOp",EDGE,"E6.3.4"),sQuery(id+"F0.wireOp",EDGE,"E6.3.5"),sQuery(id+"F0.wireOp",EDGE,"E6.3.6"),sQuery(id+"F0.wireOp",EDGE,"E6.3.7"),sQuery(id+"F0.wireOp",EDGE,"E6.3.8"),subQ1,sQuery(id+"F0.wireOp",EDGE,"E6.4.1"),sQuery(id+"F0.wireOp",EDGE,"E6.4.2"),sQuery(id+"F0.wireOp",EDGE,"E6.4.3"),sQuery(id+"F0.wireOp",EDGE,"E6.4.4"),sQuery(id+"F0.wireOp",EDGE,"E6.4.5"),sQuery(id+"F0.wireOp",EDGE,"E6.4.6"),sQuery(id+"F0.wireOp",EDGE,"E6.4.7"),sQuery(id+"F0.wireOp",EDGE,"E6.4.8"),sQuery(id+"F0.wireOp",EDGE,"E6.5.0"),sQuery(id+"F0.wireOp",EDGE,"E6.5.1"),subQ0,sQuery(id+"F0.wireOp",EDGE,"E6.5.3"),sQuery(id+"F0.wireOp",EDGE,"E6.5.4"),sQuery(id+"F0.wireOp",EDGE,"E6.5.5"),sQuery(id+"F0.wireOp",EDGE,"E6.5.6"),sQuery(id+"F0.wireOp",EDGE,"E6.5.7"),sQuery(id+"F0.wireOp",EDGE,"E6.5.8")])],"isStart":true})]});}
            var Q23;
            {var subQ0=sQuery(id+"F0.wireOp",EDGE,"E6.4.2");var subQ1=sQuery(id+"F0.wireOp",EDGE,"E6.3.0");Q23=makeQuery(id+"F2.opFillet","BLEND_EDGE",EDGE,{"blendedFrom":[makeQuery(id+"F1.opExtrude","SWEPT_EDGE",EDGE,{"disambiguationData":[OSD([subQ1,subQ0])]}),makeQuery(id+"F1.opExtrude","CAP_FACE",FACE,{"disambiguationData":[OSD([sQuery(id+"F0.wireOp",EDGE,"E0"),sQuery(id+"F0.wireOp",EDGE,"E1.0"),sQuery(id+"F0.wireOp",EDGE,"E1.1"),sQuery(id+"F0.wireOp",EDGE,"E1.2"),sQuery(id+"F0.wireOp",EDGE,"E1.3"),sQuery(id+"F0.wireOp",EDGE,"E1.4"),sQuery(id+"F0.wireOp",EDGE,"E1.5"),sQuery(id+"F0.wireOp",EDGE,"E2"),sQuery(id+"F0.wireOp",EDGE,"E3"),sQuery(id+"F0.wireOp",EDGE,"E4"),sQuery(id+"F0.wireOp",EDGE,"E6.1.0"),sQuery(id+"F0.wireOp",EDGE,"E6.1.1"),sQuery(id+"F0.wireOp",EDGE,"E6.1.2"),sQuery(id+"F0.wireOp",EDGE,"E6.1.3"),sQuery(id+"F0.wireOp",EDGE,"E6.1.4"),sQuery(id+"F0.wireOp",EDGE,"E6.1.5"),sQuery(id+"F0.wireOp",EDGE,"E6.1.6"),sQuery(id+"F0.wireOp",EDGE,"E6.1.7"),sQuery(id+"F0.wireOp",EDGE,"E6.1.8"),sQuery(id+"F0.wireOp",EDGE,"E6.2.0"),sQuery(id+"F0.wireOp",EDGE,"E6.2.1"),sQuery(id+"F0.wireOp",EDGE,"E6.2.2"),sQuery(id+"F0.wireOp",EDGE,"E6.2.3"),sQuery(id+"F0.wireOp",EDGE,"E6.2.4"),sQuery(id+"F0.wireOp",EDGE,"E6.2.5"),sQuery(id+"F0.wireOp",EDGE,"E6.2.6"),sQuery(id+"F0.wireOp",EDGE,"E6.2.7"),sQuery(id+"F0.wireOp",EDGE,"E6.2.8"),subQ1,sQuery(id+"F0.wireOp",EDGE,"E6.3.1"),sQuery(id+"F0.wireOp",EDGE,"E6.3.2"),sQuery(id+"F0.wireOp",EDGE,"E6.3.3"),sQuery(id+"F0.wireOp",EDGE,"E6.3.4"),sQuery(id+"F0.wireOp",EDGE,"E6.3.5"),sQuery(id+"F0.wireOp",EDGE,"E6.3.6"),sQuery(id+"F0.wireOp",EDGE,"E6.3.7"),sQuery(id+"F0.wireOp",EDGE,"E6.3.8"),sQuery(id+"F0.wireOp",EDGE,"E6.4.0"),sQuery(id+"F0.wireOp",EDGE,"E6.4.1"),subQ0,sQuery(id+"F0.wireOp",EDGE,"E6.4.3"),sQuery(id+"F0.wireOp",EDGE,"E6.4.4"),sQuery(id+"F0.wireOp",EDGE,"E6.4.5"),sQuery(id+"F0.wireOp",EDGE,"E6.4.6"),sQuery(id+"F0.wireOp",EDGE,"E6.4.7"),sQuery(id+"F0.wireOp",EDGE,"E6.4.8"),sQuery(id+"F0.wireOp",EDGE,"E6.5.0"),sQuery(id+"F0.wireOp",EDGE,"E6.5.1"),sQuery(id+"F0.wireOp",EDGE,"E6.5.2"),sQuery(id+"F0.wireOp",EDGE,"E6.5.3"),sQuery(id+"F0.wireOp",EDGE,"E6.5.4"),sQuery(id+"F0.wireOp",EDGE,"E6.5.5"),sQuery(id+"F0.wireOp",EDGE,"E6.5.6"),sQuery(id+"F0.wireOp",EDGE,"E6.5.7"),sQuery(id+"F0.wireOp",EDGE,"E6.5.8")])],"isStart":true})],"blendedInto":[makeQuery(id+"F1.opExtrude","CAP_FACE",FACE,{"disambiguationData":[OSD([sQuery(id+"F0.wireOp",EDGE,"E0"),sQuery(id+"F0.wireOp",EDGE,"E1.0"),sQuery(id+"F0.wireOp",EDGE,"E1.1"),sQuery(id+"F0.wireOp",EDGE,"E1.2"),sQuery(id+"F0.wireOp",EDGE,"E1.3"),sQuery(id+"F0.wireOp",EDGE,"E1.4"),sQuery(id+"F0.wireOp",EDGE,"E1.5"),sQuery(id+"F0.wireOp",EDGE,"E2"),sQuery(id+"F0.wireOp",EDGE,"E3"),sQuery(id+"F0.wireOp",EDGE,"E4"),sQuery(id+"F0.wireOp",EDGE,"E6.1.0"),sQuery(id+"F0.wireOp",EDGE,"E6.1.1"),sQuery(id+"F0.wireOp",EDGE,"E6.1.2"),sQuery(id+"F0.wireOp",EDGE,"E6.1.3"),sQuery(id+"F0.wireOp",EDGE,"E6.1.4"),sQuery(id+"F0.wireOp",EDGE,"E6.1.5"),sQuery(id+"F0.wireOp",EDGE,"E6.1.6"),sQuery(id+"F0.wireOp",EDGE,"E6.1.7"),sQuery(id+"F0.wireOp",EDGE,"E6.1.8"),sQuery(id+"F0.wireOp",EDGE,"E6.2.0"),sQuery(id+"F0.wireOp",EDGE,"E6.2.1"),sQuery(id+"F0.wireOp",EDGE,"E6.2.2"),sQuery(id+"F0.wireOp",EDGE,"E6.2.3"),sQuery(id+"F0.wireOp",EDGE,"E6.2.4"),sQuery(id+"F0.wireOp",EDGE,"E6.2.5"),sQuery(id+"F0.wireOp",EDGE,"E6.2.6"),sQuery(id+"F0.wireOp",EDGE,"E6.2.7"),sQuery(id+"F0.wireOp",EDGE,"E6.2.8"),subQ1,sQuery(id+"F0.wireOp",EDGE,"E6.3.1"),sQuery(id+"F0.wireOp",EDGE,"E6.3.2"),sQuery(id+"F0.wireOp",EDGE,"E6.3.3"),sQuery(id+"F0.wireOp",EDGE,"E6.3.4"),sQuery(id+"F0.wireOp",EDGE,"E6.3.5"),sQuery(id+"F0.wireOp",EDGE,"E6.3.6"),sQuery(id+"F0.wireOp",EDGE,"E6.3.7"),sQuery(id+"F0.wireOp",EDGE,"E6.3.8"),sQuery(id+"F0.wireOp",EDGE,"E6.4.0"),sQuery(id+"F0.wireOp",EDGE,"E6.4.1"),subQ0,sQuery(id+"F0.wireOp",EDGE,"E6.4.3"),sQuery(id+"F0.wireOp",EDGE,"E6.4.4"),sQuery(id+"F0.wireOp",EDGE,"E6.4.5"),sQuery(id+"F0.wireOp",EDGE,"E6.4.6"),sQuery(id+"F0.wireOp",EDGE,"E6.4.7"),sQuery(id+"F0.wireOp",EDGE,"E6.4.8"),sQuery(id+"F0.wireOp",EDGE,"E6.5.0"),sQuery(id+"F0.wireOp",EDGE,"E6.5.1"),sQuery(id+"F0.wireOp",EDGE,"E6.5.2"),sQuery(id+"F0.wireOp",EDGE,"E6.5.3"),sQuery(id+"F0.wireOp",EDGE,"E6.5.4"),sQuery(id+"F0.wireOp",EDGE,"E6.5.5"),sQuery(id+"F0.wireOp",EDGE,"E6.5.6"),sQuery(id+"F0.wireOp",EDGE,"E6.5.7"),sQuery(id+"F0.wireOp",EDGE,"E6.5.8")])],"isStart":true})]});}
            fillet(context, id + "F3", {"entities" : qUnion([Q0, Q1, Q2, Q3, Q4, Q5, Q6, Q7, Q8, Q9, Q10, Q11, Q12, Q13, Q14, Q15, Q16, Q17, Q18, Q19, Q20, Q21, Q22, Q23]), "radius" : 2 * mm, "tangentPropagation" : true, "allowEdgeOverflow" : false});
        }
    });
